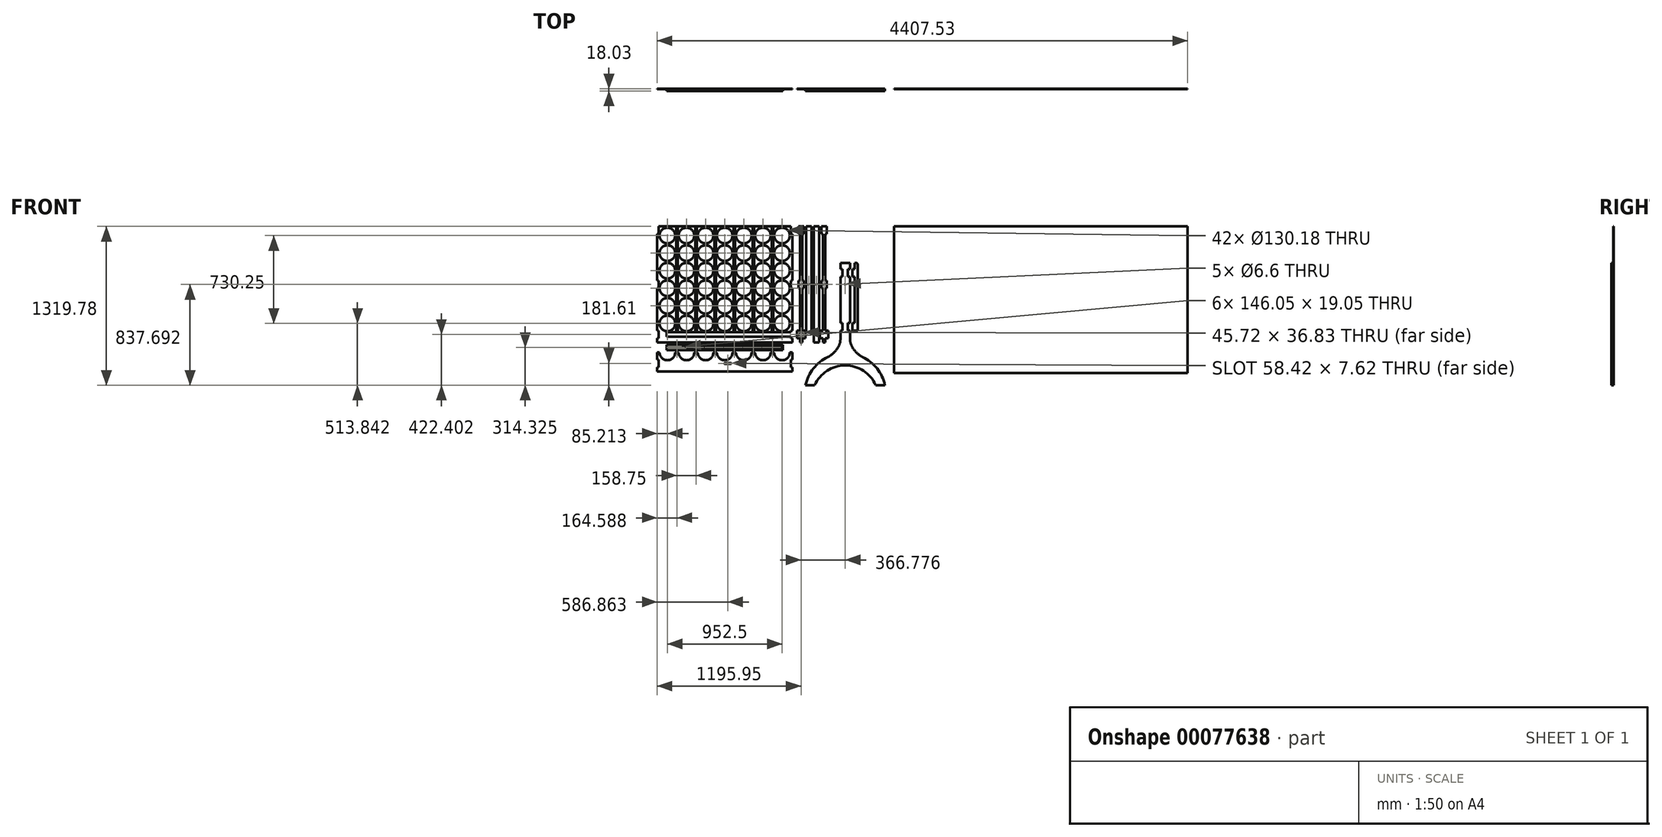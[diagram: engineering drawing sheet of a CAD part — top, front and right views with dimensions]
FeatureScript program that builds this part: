
annotation { "Feature Type Name" : "Feature", "Feature Type Description" : "" }
export const myFeature = defineFeature(function(context is Context, id is Id, definition is map)
    precondition{}
    {
        {
            assignVariable(context, id + "F0", {"name" : "Thickness", "anyValue" : .48});
        }
        {
            var Q0;
            Q0=qCreatedBy(makeId("Front.planeOp"),FACE);
            var sketch = newSketch(context, id + "F1", { "sketchPlane" : qUnion([Q0])});
            skLineSegment(sketch, "E0.bottom", {"start": v(-1389.63, 595.88) * mm, "end": v(-266.7, 595.88) * mm});
            skLineSegment(sketch, "E0.top", {"start": v(-1389.63, -368.3) * mm, "end": v(-266.7, -368.3) * mm});
            skLineSegment(sketch, "E0.left", {"start": v(-1389.63, 595.88) * mm, "end": v(-1389.63, -368.3) * mm});
            skLineSegment(sketch, "E0.right", {"start": v(-266.7, 595.88) * mm, "end": v(-266.7, -368.3) * mm});
            skCircle(sketch, "E1", {"center": v(-1304.42, 520.2) * mm, "radius": 65.09 * mm});
            skLineSegment(sketch, "E2.bottom", {"start": v(-1389.63, 595.88) * mm, "end": v(-1377.44, 595.88) * mm});
            skLineSegment(sketch, "E2.right", {"start": v(-1377.44, 595.88) * mm, "end": v(-1377.44, -368.3) * mm, "construction": true});
            skLineSegment(sketch, "E3.0", {"start": v(-278.9, 595.88) * mm, "end": v(-278.9, -368.3) * mm, "construction": true});
            skLineSegment(sketch, "E4.top", {"start": v(-1389.63, 532.38) * mm, "end": v(-1377.44, 532.38) * mm});
            skLineSegment(sketch, "E4.left", {"start": v(-1389.63, 595.88) * mm, "end": v(-1389.63, 532.38) * mm});
            skLineSegment(sketch, "E4.right", {"start": v(-1377.44, 595.88) * mm, "end": v(-1377.44, 532.38) * mm});
            skLineSegment(sketch, "E5.bottom", {"start": v(-266.7, 595.88) * mm, "end": v(-278.9, 595.88) * mm});
            skLineSegment(sketch, "E5.top", {"start": v(-266.7, 532.38) * mm, "end": v(-278.9, 532.38) * mm});
            skLineSegment(sketch, "E5.left", {"start": v(-266.7, 595.88) * mm, "end": v(-266.7, 532.38) * mm});
            skLineSegment(sketch, "E5.right", {"start": v(-278.9, 595.88) * mm, "end": v(-278.9, 532.38) * mm});
            skLineSegment(sketch, "E6.top", {"start": v(-266.7, -269.75) * mm, "end": v(-278.9, -269.75) * mm});
            skLineSegment(sketch, "E6.left", {"start": v(-266.7, -368.3) * mm, "end": v(-266.7, -269.75) * mm});
            skLineSegment(sketch, "E6.right", {"start": v(-278.9, -333.25) * mm, "end": v(-278.9, -269.75) * mm});
            skLineSegment(sketch, "E7.bottom", {"start": v(-1389.63, 145.54) * mm, "end": v(-1377.44, 145.54) * mm});
            skLineSegment(sketch, "E7.top", {"start": v(-1389.63, 82.04) * mm, "end": v(-1377.44, 82.04) * mm});
            skLineSegment(sketch, "E7.left", {"start": v(-1389.63, 145.54) * mm, "end": v(-1389.63, 82.04) * mm});
            skLineSegment(sketch, "E7.right", {"start": v(-1377.44, 145.54) * mm, "end": v(-1377.44, 82.04) * mm});
            skPoint(sketch, "E8", {"position": v(-1389.63, 113.8) * mm});
            skLineSegment(sketch, "E9.MirrorCS", {"start": v(-266.7, 82.04) * mm, "end": v(-278.9, 82.04) * mm});
            skLineSegment(sketch, "E10.MirrorCS", {"start": v(-266.7, 145.54) * mm, "end": v(-278.9, 145.54) * mm});
            skLineSegment(sketch, "E11.MirrorCS", {"start": v(-266.7, 145.54) * mm, "end": v(-266.7, 82.04) * mm});
            skLineSegment(sketch, "E12.MirrorCS", {"start": v(-278.9, 145.54) * mm, "end": v(-278.9, 82.04) * mm});
            skLineSegment(sketch, "E13", {"start": v(-1377.44, -283.08) * mm, "end": v(-278.9, -283.08) * mm});
            skLineSegment(sketch, "E14", {"start": v(-1231.4, 595.88) * mm, "end": v(-1231.4, -283.08) * mm});
            skLineSegment(sketch, "E15", {"start": v(-1218.7, 595.88) * mm, "end": v(-1218.7, -283.08) * mm});
            skLineSegment(sketch, "E16.1.0.0", {"start": v(-1059.94, 595.88) * mm, "end": v(-1059.94, -283.08) * mm});
            skLineSegment(sketch, "E16.1.0.1", {"start": v(-1072.64, 595.88) * mm, "end": v(-1072.64, -283.08) * mm});
            skLineSegment(sketch, "E16.2.0.0", {"start": v(-901.2, 595.88) * mm, "end": v(-901.2, -283.08) * mm});
            skLineSegment(sketch, "E16.2.0.1", {"start": v(-913.9, 595.88) * mm, "end": v(-913.9, -283.08) * mm});
            skLineSegment(sketch, "E16.3.0.0", {"start": v(-742.44, 595.88) * mm, "end": v(-742.44, -283.08) * mm});
            skLineSegment(sketch, "E16.3.0.1", {"start": v(-755.14, 595.88) * mm, "end": v(-755.14, -283.08) * mm});
            skLineSegment(sketch, "E16.4.0.0", {"start": v(-583.7, 595.88) * mm, "end": v(-583.7, -283.08) * mm});
            skLineSegment(sketch, "E16.4.0.1", {"start": v(-596.4, 595.88) * mm, "end": v(-596.4, -283.08) * mm});
            skLineSegment(sketch, "E16.5.0.0", {"start": v(-424.94, 595.88) * mm, "end": v(-424.94, -283.08) * mm});
            skLineSegment(sketch, "E16.5.0.1", {"start": v(-437.64, 595.88) * mm, "end": v(-437.64, -283.08) * mm});
            skLineSegment(sketch, "E16.direction1", {"start": v(-1218.7, -283.08) * mm, "end": v(-1059.94, -283.08) * mm, "construction": true});
            skLineSegment(sketch, "E17.bottom", {"start": v(-1304.42, -387.35) * mm, "end": v(-351.92, -387.35) * mm});
            skLineSegment(sketch, "E17.top", {"start": v(-1304.42, -431.8) * mm, "end": v(-351.92, -431.8) * mm});
            skLineSegment(sketch, "E17.left", {"start": v(-1304.42, -387.35) * mm, "end": v(-1304.42, -431.8) * mm, "construction": true});
            skLineSegment(sketch, "E17.right", {"start": v(-351.92, -387.35) * mm, "end": v(-351.92, -431.8) * mm, "construction": true});
            skLineSegment(sketch, "E18.bottom", {"start": v(-1298.07, -387.35) * mm, "end": v(-1310.77, -387.35) * mm});
            skLineSegment(sketch, "E18.top", {"start": v(-1298.07, -431.8) * mm, "end": v(-1310.77, -431.8) * mm});
            skLineSegment(sketch, "E18.left", {"start": v(-1298.07, -387.35) * mm, "end": v(-1298.07, -431.8) * mm});
            skLineSegment(sketch, "E18.right", {"start": v(-1310.77, -387.35) * mm, "end": v(-1310.77, -431.8) * mm});
            skPoint(sketch, "E18.middle", {"position": v(-1304.42, -409.57) * mm});
            skLineSegment(sketch, "E19.1.0.0", {"start": v(-1139.32, -387.35) * mm, "end": v(-1139.32, -431.8) * mm});
            skLineSegment(sketch, "E19.1.0.1", {"start": v(-1152.02, -387.35) * mm, "end": v(-1152.02, -431.8) * mm});
            skLineSegment(sketch, "E19.2.0.0", {"start": v(-980.57, -387.35) * mm, "end": v(-980.57, -431.8) * mm});
            skLineSegment(sketch, "E19.2.0.1", {"start": v(-993.27, -387.35) * mm, "end": v(-993.27, -431.8) * mm});
            skLineSegment(sketch, "E19.3.0.0", {"start": v(-821.82, -387.35) * mm, "end": v(-821.82, -431.8) * mm});
            skLineSegment(sketch, "E19.3.0.1", {"start": v(-834.52, -387.35) * mm, "end": v(-834.52, -431.8) * mm});
            skLineSegment(sketch, "E19.4.0.0", {"start": v(-663.07, -387.35) * mm, "end": v(-663.07, -431.8) * mm});
            skLineSegment(sketch, "E19.4.0.1", {"start": v(-675.77, -387.35) * mm, "end": v(-675.77, -431.8) * mm});
            skLineSegment(sketch, "E19.5.0.0", {"start": v(-504.32, -387.35) * mm, "end": v(-504.32, -431.8) * mm});
            skLineSegment(sketch, "E19.5.0.1", {"start": v(-517.02, -387.35) * mm, "end": v(-517.02, -431.8) * mm});
            skLineSegment(sketch, "E19.6.0.0", {"start": v(-345.57, -387.35) * mm, "end": v(-345.57, -431.8) * mm});
            skLineSegment(sketch, "E19.6.0.1", {"start": v(-358.27, -387.35) * mm, "end": v(-358.27, -431.8) * mm});
            skLineSegment(sketch, "E19.direction1", {"start": v(-1298.07, -431.8) * mm, "end": v(-1139.32, -431.8) * mm, "construction": true});
            skLineSegment(sketch, "E20", {"start": v(-345.57, -387.35) * mm, "end": v(-351.92, -387.35) * mm});
            skLineSegment(sketch, "E21", {"start": v(-321.75, -431.8) * mm, "end": v(-351.92, -431.8) * mm});
            skLineSegment(sketch, "E22", {"start": v(-1298.07, -409.58) * mm, "end": v(-1152.02, -409.58) * mm, "construction": true});
            skLineSegment(sketch, "E23.0", {"start": v(-1298.07, -419.1) * mm, "end": v(-1152.02, -419.1) * mm});
            skLineSegment(sketch, "E24.0", {"start": v(-1298.07, -400.05) * mm, "end": v(-1152.02, -400.05) * mm});
            skLineSegment(sketch, "E25.1.0.0", {"start": v(-1139.32, -400.05) * mm, "end": v(-993.27, -400.05) * mm});
            skLineSegment(sketch, "E25.1.0.1", {"start": v(-1139.32, -419.1) * mm, "end": v(-993.27, -419.1) * mm});
            skLineSegment(sketch, "E25.2.0.0", {"start": v(-980.57, -400.05) * mm, "end": v(-834.52, -400.05) * mm});
            skLineSegment(sketch, "E25.2.0.1", {"start": v(-980.57, -419.1) * mm, "end": v(-834.52, -419.1) * mm});
            skLineSegment(sketch, "E25.3.0.0", {"start": v(-821.82, -400.05) * mm, "end": v(-675.77, -400.05) * mm});
            skLineSegment(sketch, "E25.3.0.1", {"start": v(-821.82, -419.1) * mm, "end": v(-675.77, -419.1) * mm});
            skLineSegment(sketch, "E25.4.0.0", {"start": v(-663.07, -400.05) * mm, "end": v(-517.02, -400.05) * mm});
            skLineSegment(sketch, "E25.4.0.1", {"start": v(-663.07, -419.1) * mm, "end": v(-517.02, -419.1) * mm});
            skLineSegment(sketch, "E25.5.0.0", {"start": v(-504.32, -400.05) * mm, "end": v(-358.27, -400.05) * mm});
            skLineSegment(sketch, "E25.5.0.1", {"start": v(-504.32, -419.1) * mm, "end": v(-358.27, -419.1) * mm});
            skLineSegment(sketch, "E25.direction1", {"start": v(-1298.07, -400.05) * mm, "end": v(-1139.32, -400.05) * mm, "construction": true});
            skLineSegment(sketch, "E26.0", {"start": v(-1377.44, -319.91) * mm, "end": v(-278.9, -319.91) * mm});
            skLineSegment(sketch, "E27", {"start": v(-278.9, -333.25) * mm, "end": v(-266.7, -333.25) * mm});
            skLineSegment(sketch, "E28", {"start": v(-828.17, -368.3) * mm, "end": v(-828.17, -319.91) * mm, "construction": true});
            skLineSegment(sketch, "E29.MirrorCS", {"start": v(-1377.44, -333.25) * mm, "end": v(-1389.63, -333.25) * mm});
            skLineSegment(sketch, "E30.MirrorCS", {"start": v(-1377.44, -333.25) * mm, "end": v(-1377.44, -269.75) * mm});
            skLineSegment(sketch, "E31.MirrorCS", {"start": v(-1389.63, -269.75) * mm, "end": v(-1377.44, -269.75) * mm});
            skLineSegment(sketch, "E32", {"start": v(-1310.77, -319.91) * mm, "end": v(-1310.77, -283.08) * mm});
            skLineSegment(sketch, "E33.bottom", {"start": v(-215.9, 595.88) * mm, "end": v(-171.45, 595.88) * mm, "construction": true});
            skLineSegment(sketch, "E34.bottom", {"start": v(-228.1, -333.25) * mm, "end": v(-203.7, -333.25) * mm});
            skLineSegment(sketch, "E34.top", {"start": v(-228.1, -269.75) * mm, "end": v(-203.7, -269.75) * mm});
            skLineSegment(sketch, "E34.left", {"start": v(-228.1, -333.25) * mm, "end": v(-228.1, -269.75) * mm});
            skLineSegment(sketch, "E34.right", {"start": v(-203.7, -333.25) * mm, "end": v(-203.7, -269.75) * mm});
            skLineSegment(sketch, "E35", {"start": v(-193.68, -368.3) * mm, "end": v(-193.68, 595.88) * mm, "construction": true});
            skLineSegment(sketch, "E36.bottom", {"start": v(-215.9, 145.54) * mm, "end": v(-203.7, 145.54) * mm});
            skLineSegment(sketch, "E36.top", {"start": v(-215.9, 82.04) * mm, "end": v(-203.7, 82.04) * mm});
            skLineSegment(sketch, "E36.left", {"start": v(-215.9, 145.54) * mm, "end": v(-215.9, 82.04) * mm});
            skLineSegment(sketch, "E36.right", {"start": v(-203.7, 145.54) * mm, "end": v(-203.7, 82.04) * mm});
            skLineSegment(sketch, "E37.bottom", {"start": v(-215.9, 595.88) * mm, "end": v(-203.7, 595.88) * mm});
            skLineSegment(sketch, "E37.top", {"start": v(-215.9, 532.38) * mm, "end": v(-203.7, 532.38) * mm});
            skLineSegment(sketch, "E37.left", {"start": v(-215.9, 595.88) * mm, "end": v(-215.9, 532.38) * mm});
            skLineSegment(sketch, "E37.right", {"start": v(-203.7, 595.88) * mm, "end": v(-203.7, 532.38) * mm});
            skLineSegment(sketch, "E38.MirrorCS", {"start": v(-171.45, 595.88) * mm, "end": v(-171.45, 532.38) * mm});
            skLineSegment(sketch, "E39.MirrorCS", {"start": v(-171.45, 595.88) * mm, "end": v(-183.64, 595.88) * mm});
            skLineSegment(sketch, "E40.MirrorCS", {"start": v(-183.64, 595.88) * mm, "end": v(-183.64, 532.38) * mm});
            skLineSegment(sketch, "E41.MirrorCS", {"start": v(-171.45, 532.38) * mm, "end": v(-183.64, 532.38) * mm});
            skLineSegment(sketch, "E42.MirrorCS", {"start": v(-171.45, 145.54) * mm, "end": v(-171.45, 82.04) * mm});
            skLineSegment(sketch, "E43.MirrorCS", {"start": v(-171.45, 82.04) * mm, "end": v(-183.64, 82.04) * mm});
            skLineSegment(sketch, "E44.MirrorCS", {"start": v(-183.64, 145.54) * mm, "end": v(-183.64, 82.04) * mm});
            skLineSegment(sketch, "E45.MirrorCS", {"start": v(-171.45, 145.54) * mm, "end": v(-183.64, 145.54) * mm});
            skLineSegment(sketch, "E46.MirrorCS", {"start": v(-159.26, -333.25) * mm, "end": v(-159.26, -269.75) * mm});
            skLineSegment(sketch, "E47.MirrorCS", {"start": v(-159.26, -333.25) * mm, "end": v(-183.64, -333.25) * mm});
            skLineSegment(sketch, "E48.MirrorCS", {"start": v(-159.26, -269.75) * mm, "end": v(-183.64, -269.75) * mm});
            skLineSegment(sketch, "E49.MirrorCS", {"start": v(-183.64, -333.25) * mm, "end": v(-183.64, -269.75) * mm});
            skLineSegment(sketch, "E50.bottom", {"start": v(-203.7, -368.3) * mm, "end": v(-183.64, -368.3) * mm});
            skLineSegment(sketch, "E50.top", {"start": v(-203.7, 595.88) * mm, "end": v(-183.64, 595.88) * mm});
            skLineSegment(sketch, "E50.left", {"start": v(-203.7, -368.3) * mm, "end": v(-203.7, 595.88) * mm});
            skLineSegment(sketch, "E50.right", {"start": v(-183.64, -368.3) * mm, "end": v(-183.64, 595.88) * mm});
            skLineSegment(sketch, "E51.bottom", {"start": v(-216.54, -283.08) * mm, "end": v(-170.82, -283.08) * mm});
            skLineSegment(sketch, "E51.top", {"start": v(-216.54, -319.91) * mm, "end": v(-170.82, -319.91) * mm});
            skLineSegment(sketch, "E51.left", {"start": v(-216.54, -283.08) * mm, "end": v(-216.54, -319.91) * mm});
            skLineSegment(sketch, "E51.right", {"start": v(-170.82, -283.08) * mm, "end": v(-170.82, -319.91) * mm});
            skPoint(sketch, "E52", {"position": v(-193.68, -283.08) * mm});
            skLineSegment(sketch, "E53.bottom", {"start": v(-152.4, 595.88) * mm, "end": v(-107.95, 595.88) * mm});
            skLineSegment(sketch, "E53.top", {"start": v(-152.4, -368.3) * mm, "end": v(-107.95, -368.3) * mm, "construction": true});
            skLineSegment(sketch, "E53.left", {"start": v(-152.4, 595.88) * mm, "end": v(-152.4, -368.3) * mm});
            skLineSegment(sketch, "E53.right", {"start": v(-107.95, 595.88) * mm, "end": v(-107.95, -368.3) * mm});
            skLineSegment(sketch, "E54.0", {"start": v(-98.43, 532.38) * mm, "end": v(-98.43, -368.3) * mm, "construction": true});
            skLineSegment(sketch, "E55.MirrorCS", {"start": v(19.05, 595.88) * mm, "end": v(6.86, 595.88) * mm});
            skLineSegment(sketch, "E56.MirrorCS", {"start": v(-25.4, 595.88) * mm, "end": v(-13.2, 595.88) * mm});
            skLineSegment(sketch, "E57.MirrorCS", {"start": v(-37.6, -333.25) * mm, "end": v(-13.2, -333.25) * mm});
            skLineSegment(sketch, "E58.MirrorCS", {"start": v(31.24, -333.25) * mm, "end": v(6.86, -333.25) * mm});
            skLineSegment(sketch, "E59.MirrorCS", {"start": v(19.05, 82.04) * mm, "end": v(6.86, 82.04) * mm});
            skLineSegment(sketch, "E60.MirrorCS", {"start": v(19.05, 532.38) * mm, "end": v(6.86, 532.38) * mm});
            skLineSegment(sketch, "E61.MirrorCS", {"start": v(19.05, 595.88) * mm, "end": v(-25.4, 595.88) * mm, "construction": true});
            skLineSegment(sketch, "E62.MirrorCS", {"start": v(-37.6, -269.75) * mm, "end": v(-13.2, -269.75) * mm});
            skLineSegment(sketch, "E63.MirrorCS", {"start": v(-25.4, 532.38) * mm, "end": v(-13.2, 532.38) * mm});
            skLineSegment(sketch, "E64.MirrorCS", {"start": v(31.24, -269.75) * mm, "end": v(6.86, -269.75) * mm});
            skLineSegment(sketch, "E65.MirrorCS", {"start": v(-25.4, 82.04) * mm, "end": v(-13.2, 82.04) * mm});
            skLineSegment(sketch, "E66.MirrorCS", {"start": v(19.05, 145.54) * mm, "end": v(6.86, 145.54) * mm});
            skLineSegment(sketch, "E67.MirrorCS", {"start": v(-25.4, 145.54) * mm, "end": v(-13.2, 145.54) * mm});
            skLineSegment(sketch, "E68.MirrorCS", {"start": v(6.86, 595.88) * mm, "end": v(-13.2, 595.88) * mm});
            skLineSegment(sketch, "E69.MirrorCS", {"start": v(6.86, 145.54) * mm, "end": v(6.86, 82.04) * mm});
            skLineSegment(sketch, "E70.MirrorCS", {"start": v(-13.2, -333.25) * mm, "end": v(-13.2, -269.75) * mm});
            skLineSegment(sketch, "E71.MirrorCS", {"start": v(6.86, -368.3) * mm, "end": v(-13.2, -368.3) * mm});
            skLineSegment(sketch, "E72.MirrorCS", {"start": v(-44.45, -368.3) * mm, "end": v(-88.9, -368.3) * mm});
            skLineSegment(sketch, "E73.MirrorCS", {"start": v(-25.4, 145.54) * mm, "end": v(-25.4, 82.04) * mm});
            skLineSegment(sketch, "E74.MirrorCS", {"start": v(-13.2, 145.54) * mm, "end": v(-13.2, 82.04) * mm});
            skLineSegment(sketch, "E75.MirrorCS", {"start": v(6.86, -333.25) * mm, "end": v(6.86, -269.75) * mm});
            skLineSegment(sketch, "E76.MirrorCS", {"start": v(-37.6, -333.25) * mm, "end": v(-37.6, -269.75) * mm});
            skLineSegment(sketch, "E77.MirrorCS", {"start": v(19.05, 145.54) * mm, "end": v(19.05, 82.04) * mm});
            skLineSegment(sketch, "E78.MirrorCS", {"start": v(-13.2, -368.3) * mm, "end": v(-13.2, 595.88) * mm});
            skLineSegment(sketch, "E79.MirrorCS", {"start": v(-13.2, 595.88) * mm, "end": v(-13.2, 532.38) * mm});
            skPoint(sketch, "E80.MirrorP", {"position": v(-3.18, -283.08) * mm});
            skLineSegment(sketch, "E81.MirrorCS", {"start": v(-25.4, 595.88) * mm, "end": v(-25.4, 532.38) * mm});
            skLineSegment(sketch, "E82.MirrorCS", {"start": v(6.86, 595.88) * mm, "end": v(6.86, 532.38) * mm});
            skLineSegment(sketch, "E83.MirrorCS", {"start": v(19.05, 595.88) * mm, "end": v(19.05, 532.38) * mm});
            skLineSegment(sketch, "E84.MirrorCS", {"start": v(6.86, -368.3) * mm, "end": v(6.86, 595.88) * mm});
            skLineSegment(sketch, "E85.MirrorCS", {"start": v(31.24, -333.25) * mm, "end": v(31.24, -269.75) * mm});
            skLineSegment(sketch, "E86.MirrorCS", {"start": v(-44.45, 595.88) * mm, "end": v(-88.9, 595.88) * mm});
            skLineSegment(sketch, "E87.MirrorCS", {"start": v(-44.45, 595.88) * mm, "end": v(-44.45, -368.3) * mm});
            skLineSegment(sketch, "E88.MirrorCS", {"start": v(-88.9, 595.88) * mm, "end": v(-88.9, -368.3) * mm});
            skLineSegment(sketch, "E89.MirrorCS", {"start": v(-3.18, -368.3) * mm, "end": v(-3.18, 595.88) * mm, "construction": true});
            skLineSegment(sketch, "E90.bottom", {"start": v(-152.4, -283.08) * mm, "end": v(-107.95, -283.08) * mm});
            skLineSegment(sketch, "E90.top", {"start": v(-152.4, -319.91) * mm, "end": v(-107.95, -319.91) * mm, "construction": true});
            skLineSegment(sketch, "E90.left", {"start": v(-152.4, -283.08) * mm, "end": v(-152.4, -319.91) * mm});
            skLineSegment(sketch, "E90.right", {"start": v(-107.95, -283.08) * mm, "end": v(-107.95, -319.91) * mm});
            skLineSegment(sketch, "E91.bottom", {"start": v(-1389.63, -450.85) * mm, "end": v(-266.7, -450.85) * mm});
            skLineSegment(sketch, "E91.top", {"start": v(-1389.63, -609.1) * mm, "end": v(-266.7, -609.1) * mm});
            skLineSegment(sketch, "E91.left", {"start": v(-1389.63, -450.85) * mm, "end": v(-1389.63, -609.1) * mm});
            skLineSegment(sketch, "E91.right", {"start": v(-266.7, -450.85) * mm, "end": v(-266.7, -609.1) * mm});
            skLineSegment(sketch, "E92.bottom", {"start": v(132.84, -368.3) * mm, "end": v(213.36, -368.3) * mm, "construction": true});
            skLineSegment(sketch, "E92.top", {"start": v(132.84, 292.1) * mm, "end": v(213.36, 292.1) * mm});
            skLineSegment(sketch, "E92.left", {"start": v(132.84, -368.3) * mm, "end": v(132.84, 292.1) * mm});
            skLineSegment(sketch, "E92.right", {"start": v(213.36, -368.3) * mm, "end": v(213.36, 292.1) * mm});
            skLineSegment(sketch, "E93", {"start": v(132.84, -368.3) * mm, "end": v(37.01, -485.83) * mm});
            skLineSegment(sketch, "E94", {"start": v(-157.1, -723.9) * mm, "end": v(503.3, -723.9) * mm});
            skLineSegment(sketch, "E95", {"start": v(503.3, -723.9) * mm, "end": v(309.19, -485.83) * mm, "construction": true});
            skLineSegment(sketch, "E96", {"start": v(173.1, -368.3) * mm, "end": v(173.1, -723.9) * mm, "construction": true});
            skLineSegment(sketch, "E97.bottom", {"start": v(132.84, -269.75) * mm, "end": v(150.88, -269.75) * mm});
            skLineSegment(sketch, "E97.top", {"start": v(132.84, -206.25) * mm, "end": v(150.88, -206.25) * mm});
            skLineSegment(sketch, "E97.left", {"start": v(132.84, -269.75) * mm, "end": v(132.84, -206.25) * mm});
            skLineSegment(sketch, "E97.right", {"start": v(150.88, -269.75) * mm, "end": v(150.88, -206.25) * mm});
            skLineSegment(sketch, "E98.bottom", {"start": v(132.84, 241.3) * mm, "end": v(150.88, 241.3) * mm});
            skLineSegment(sketch, "E98.top", {"start": v(132.84, 177.8) * mm, "end": v(150.88, 177.8) * mm});
            skLineSegment(sketch, "E98.left", {"start": v(132.84, 241.3) * mm, "end": v(132.84, 177.8) * mm});
            skLineSegment(sketch, "E98.right", {"start": v(150.88, 241.3) * mm, "end": v(150.88, 177.8) * mm});
            skLineSegment(sketch, "E99.MirrorCS", {"start": v(213.36, -269.75) * mm, "end": v(195.33, -269.75) * mm});
            skLineSegment(sketch, "E100.MirrorCS", {"start": v(213.36, -206.25) * mm, "end": v(195.33, -206.25) * mm});
            skLineSegment(sketch, "E101.MirrorCS", {"start": v(213.36, -269.75) * mm, "end": v(213.36, -206.25) * mm});
            skLineSegment(sketch, "E102.MirrorCS", {"start": v(195.33, -269.75) * mm, "end": v(195.33, -206.25) * mm});
            skLineSegment(sketch, "E103.MirrorCS", {"start": v(213.36, 241.3) * mm, "end": v(213.36, 177.8) * mm});
            skLineSegment(sketch, "E104.MirrorCS", {"start": v(213.36, 177.8) * mm, "end": v(195.33, 177.8) * mm});
            skLineSegment(sketch, "E105.MirrorCS", {"start": v(195.33, 241.3) * mm, "end": v(195.33, 177.8) * mm});
            skLineSegment(sketch, "E106.MirrorCS", {"start": v(213.36, 241.3) * mm, "end": v(195.33, 241.3) * mm});
            skLineSegment(sketch, "E107.bottom", {"start": v(250.44, 292.1) * mm, "end": v(275.84, 292.1) * mm});
            skLineSegment(sketch, "E107.top", {"start": v(250.44, -269.75) * mm, "end": v(275.84, -269.75) * mm});
            skLineSegment(sketch, "E107.left", {"start": v(250.44, 292.1) * mm, "end": v(250.44, -269.75) * mm});
            skLineSegment(sketch, "E107.right", {"start": v(275.84, 292.1) * mm, "end": v(275.84, -269.75) * mm});
            skLineSegment(sketch, "E108.bottom", {"start": v(250.44, -269.75) * mm, "end": v(232.4, -269.75) * mm});
            skLineSegment(sketch, "E108.top", {"start": v(250.44, -206.25) * mm, "end": v(232.4, -206.25) * mm});
            skLineSegment(sketch, "E108.left", {"start": v(250.44, -269.75) * mm, "end": v(250.44, -206.25) * mm});
            skLineSegment(sketch, "E108.right", {"start": v(232.4, -269.75) * mm, "end": v(232.4, -206.25) * mm});
            skLineSegment(sketch, "E109.bottom", {"start": v(250.44, 241.3) * mm, "end": v(232.4, 241.3) * mm});
            skLineSegment(sketch, "E109.top", {"start": v(250.44, 177.8) * mm, "end": v(232.4, 177.8) * mm});
            skLineSegment(sketch, "E109.left", {"start": v(250.44, 241.3) * mm, "end": v(250.44, 177.8) * mm});
            skLineSegment(sketch, "E109.right", {"start": v(232.4, 241.3) * mm, "end": v(232.4, 177.8) * mm});
            skCircle(sketch, "E110", {"center": v(-3.18, 113.8) * mm, "radius": 3.3 * mm});
            skLineSegment(sketch, "E111", {"start": v(173.1, 292.1) * mm, "end": v(173.1, 113.8) * mm, "construction": true});
            skCircle(sketch, "E112", {"center": v(173.1, 113.8) * mm, "radius": 3.3 * mm});
            skCircle(sketch, "E113.MirrorC", {"center": v(-193.68, 113.8) * mm, "radius": 3.3 * mm});
            skCircle(sketch, "E114", {"center": v(-66.68, 113.8) * mm, "radius": 3.3 * mm});
            skPoint(sketch, "E114.centerSnap0", {"position": v(-25.4, 113.8) * mm});
            skPoint(sketch, "E114.centerSnap1", {"position": v(-66.68, 595.88) * mm});
            skCircle(sketch, "E115.MirrorC", {"center": v(-130.18, 113.8) * mm, "radius": 3.3 * mm});
            skLineSegment(sketch, "E116.top", {"start": v(-80.9, -711.2) * mm, "end": v(427.1, -711.2) * mm, "construction": true});
            skLineSegment(sketch, "E116.left", {"start": v(-80.9, -723.9) * mm, "end": v(-80.9, -711.2) * mm});
            skLineSegment(sketch, "E116.right", {"start": v(427.1, -723.9) * mm, "end": v(427.1, -711.2) * mm});
            skPoint(sketch, "E117", {"position": v(173.1, -711.2) * mm});
            skPoint(sketch, "E118", {"position": v(-130.18, -319.91) * mm});
            skLineSegment(sketch, "E119", {"start": v(-130.18, -368.3) * mm, "end": v(-130.18, -269.75) * mm, "construction": true});
            skArc(sketch, "E120", {"start": v(503.3, -723.9) * mm, "mid": v(173.1, -457.2) * mm, "end": v(-157.1, -723.9) * mm});
            skLineSegment(sketch, "E121", {"start": v(37.01, -485.83) * mm, "end": v(-157.1, -723.9) * mm, "construction": true});
            skLineSegment(sketch, "E122", {"start": v(309.19, -485.83) * mm, "end": v(213.36, -368.3) * mm});
            skArc(sketch, "E123", {"start": v(37.01, -485.83) * mm, "mid": v(94.77, -435.09) * mm, "end": v(132.84, -368.3) * mm});
            skArc(sketch, "E124", {"start": v(427.1, -723.9) * mm, "mid": v(173.1, -558.8) * mm, "end": v(-80.9, -723.9) * mm});
            skArc(sketch, "E125.MirrorCS", {"start": v(309.19, -485.83) * mm, "mid": v(251.43, -435.09) * mm, "end": v(213.36, -368.3) * mm});
            skArc(sketch, "E126.MirrorC", {"start": v(-445.58, -450.85) * mm, "mid": v(-510.67, -515.94) * mm, "end": v(-575.75, -450.85) * mm});
            skArc(sketch, "E127.MirrorC", {"start": v(-286.83, -450.85) * mm, "mid": v(-351.92, -515.94) * mm, "end": v(-417, -450.85) * mm});
            skArc(sketch, "E128.trimOffspring", {"start": v(-1239.33, -450.85) * mm, "mid": v(-1304.42, -515.94) * mm, "end": v(-1369.5, -450.85) * mm});
            skArc(sketch, "E129.trimOffspring", {"start": v(-1080.58, -450.85) * mm, "mid": v(-1145.67, -515.94) * mm, "end": v(-1210.75, -450.85) * mm});
            skArc(sketch, "E130.trimOffspring", {"start": v(-921.83, -450.85) * mm, "mid": v(-986.92, -515.94) * mm, "end": v(-1052, -450.85) * mm});
            skArc(sketch, "E131.trimOffspring", {"start": v(-763.08, -450.85) * mm, "mid": v(-828.17, -515.94) * mm, "end": v(-893.25, -450.85) * mm});
            skArc(sketch, "E132.trimOffspring", {"start": v(-604.33, -450.85) * mm, "mid": v(-669.42, -515.94) * mm, "end": v(-734.5, -450.85) * mm});
            skLineSegment(sketch, "E133.bottom", {"start": v(-1389.63, -510.54) * mm, "end": v(-1376.43, -510.54) * mm});
            skLineSegment(sketch, "E133.top", {"start": v(-1389.63, -450.85) * mm, "end": v(-1376.43, -450.85) * mm});
            skLineSegment(sketch, "E133.left", {"start": v(-1389.63, -510.54) * mm, "end": v(-1389.63, -450.85) * mm, "construction": true});
            skLineSegment(sketch, "E133.right", {"start": v(-1376.43, -510.54) * mm, "end": v(-1376.43, -450.85) * mm});
            skLineSegment(sketch, "E134.bottom", {"start": v(-1389.63, -450.85) * mm, "end": v(-1401.83, -450.85) * mm, "construction": true});
            skLineSegment(sketch, "E134.top", {"start": v(-1389.63, -510.54) * mm, "end": v(-1401.83, -510.54) * mm, "construction": true});
            skLineSegment(sketch, "E134.left", {"start": v(-1389.63, -450.85) * mm, "end": v(-1389.63, -510.54) * mm, "construction": true});
            skLineSegment(sketch, "E134.right", {"start": v(-1401.83, -450.85) * mm, "end": v(-1401.83, -510.54) * mm, "construction": true});
            skLineSegment(sketch, "E135.MirrorCS", {"start": v(-279.9, -510.54) * mm, "end": v(-279.9, -450.85) * mm});
            skLineSegment(sketch, "E136", {"start": v(-279.9, -510.54) * mm, "end": v(-266.7, -510.54) * mm});
            skLineSegment(sketch, "E137.top", {"start": v(-279.9, -574.04) * mm, "end": v(-266.7, -574.04) * mm});
            skLineSegment(sketch, "E137.left", {"start": v(-279.9, -510.54) * mm, "end": v(-279.9, -574.04) * mm});
            skLineSegment(sketch, "E137.right", {"start": v(-266.7, -510.54) * mm, "end": v(-266.7, -574.04) * mm});
            skLineSegment(sketch, "E138.MirrorCS", {"start": v(-1376.43, -510.54) * mm, "end": v(-1376.43, -574.04) * mm});
            skLineSegment(sketch, "E139.MirrorCS", {"start": v(-1376.43, -574.04) * mm, "end": v(-1389.63, -574.04) * mm});
            skLineSegment(sketch, "E140", {"start": v(-828.17, -542.29) * mm, "end": v(-777.37, -542.29) * mm});
            skArc(sketch, "E141.0.startCap", {"start": v(-828.17, -546.1) * mm, "mid": v(-831.98, -542.29) * mm, "end": v(-828.17, -538.48) * mm});
            skArc(sketch, "E141.0.endCap", {"start": v(-777.37, -538.48) * mm, "mid": v(-773.56, -542.29) * mm, "end": v(-777.37, -546.1) * mm});
            skLineSegment(sketch, "E141.0.left", {"start": v(-828.17, -538.48) * mm, "end": v(-777.37, -538.48) * mm});
            skLineSegment(sketch, "E141.0.right", {"start": v(-828.17, -546.1) * mm, "end": v(-777.37, -546.1) * mm});
            skCircle(sketch, "E142.0.1.0", {"center": v(-1304.42, 374.14) * mm, "radius": 65.09 * mm});
            skCircle(sketch, "E142.0.2.0", {"center": v(-1304.42, 228.1) * mm, "radius": 65.09 * mm});
            skCircle(sketch, "E142.0.3.0", {"center": v(-1304.42, 82.04) * mm, "radius": 65.09 * mm});
            skCircle(sketch, "E142.0.4.0", {"center": v(-1304.42, -64) * mm, "radius": 65.09 * mm});
            skCircle(sketch, "E142.0.5.0", {"center": v(-1304.42, -210.06) * mm, "radius": 65.09 * mm});
            skCircle(sketch, "E142.1.0.0", {"center": v(-1145.67, 520.2) * mm, "radius": 65.09 * mm});
            skCircle(sketch, "E142.1.1.0", {"center": v(-1145.67, 374.14) * mm, "radius": 65.09 * mm});
            skCircle(sketch, "E142.1.2.0", {"center": v(-1145.67, 228.1) * mm, "radius": 65.09 * mm});
            skCircle(sketch, "E142.1.3.0", {"center": v(-1145.67, 82.04) * mm, "radius": 65.09 * mm});
            skCircle(sketch, "E142.1.4.0", {"center": v(-1145.67, -64) * mm, "radius": 65.09 * mm});
            skCircle(sketch, "E142.1.5.0", {"center": v(-1145.67, -210.06) * mm, "radius": 65.09 * mm});
            skCircle(sketch, "E142.2.0.0", {"center": v(-986.92, 520.2) * mm, "radius": 65.09 * mm});
            skCircle(sketch, "E142.2.1.0", {"center": v(-986.92, 374.14) * mm, "radius": 65.09 * mm});
            skCircle(sketch, "E142.2.2.0", {"center": v(-986.92, 228.1) * mm, "radius": 65.09 * mm});
            skCircle(sketch, "E142.2.3.0", {"center": v(-986.92, 82.04) * mm, "radius": 65.09 * mm});
            skCircle(sketch, "E142.2.4.0", {"center": v(-986.92, -64) * mm, "radius": 65.09 * mm});
            skCircle(sketch, "E142.2.5.0", {"center": v(-986.92, -210.06) * mm, "radius": 65.09 * mm});
            skCircle(sketch, "E142.3.0.0", {"center": v(-828.17, 520.2) * mm, "radius": 65.09 * mm});
            skCircle(sketch, "E142.3.1.0", {"center": v(-828.17, 374.14) * mm, "radius": 65.09 * mm});
            skCircle(sketch, "E142.3.2.0", {"center": v(-828.17, 228.1) * mm, "radius": 65.09 * mm});
            skCircle(sketch, "E142.3.3.0", {"center": v(-828.17, 82.04) * mm, "radius": 65.09 * mm});
            skCircle(sketch, "E142.3.4.0", {"center": v(-828.17, -64) * mm, "radius": 65.09 * mm});
            skCircle(sketch, "E142.3.5.0", {"center": v(-828.17, -210.06) * mm, "radius": 65.09 * mm});
            skCircle(sketch, "E142.4.0.0", {"center": v(-669.42, 520.2) * mm, "radius": 65.09 * mm});
            skCircle(sketch, "E142.4.1.0", {"center": v(-669.42, 374.14) * mm, "radius": 65.09 * mm});
            skCircle(sketch, "E142.4.2.0", {"center": v(-669.42, 228.1) * mm, "radius": 65.09 * mm});
            skCircle(sketch, "E142.4.3.0", {"center": v(-669.42, 82.04) * mm, "radius": 65.09 * mm});
            skCircle(sketch, "E142.4.4.0", {"center": v(-669.42, -64) * mm, "radius": 65.09 * mm});
            skCircle(sketch, "E142.4.5.0", {"center": v(-669.42, -210.06) * mm, "radius": 65.09 * mm});
            skCircle(sketch, "E142.5.0.0", {"center": v(-510.67, 520.2) * mm, "radius": 65.09 * mm});
            skCircle(sketch, "E142.5.1.0", {"center": v(-510.67, 374.14) * mm, "radius": 65.09 * mm});
            skCircle(sketch, "E142.5.2.0", {"center": v(-510.67, 228.1) * mm, "radius": 65.09 * mm});
            skCircle(sketch, "E142.5.3.0", {"center": v(-510.67, 82.04) * mm, "radius": 65.09 * mm});
            skCircle(sketch, "E142.5.4.0", {"center": v(-510.67, -64) * mm, "radius": 65.09 * mm});
            skCircle(sketch, "E142.5.5.0", {"center": v(-510.67, -210.06) * mm, "radius": 65.09 * mm});
            skCircle(sketch, "E142.6.0.0", {"center": v(-351.92, 520.2) * mm, "radius": 65.09 * mm});
            skCircle(sketch, "E142.6.1.0", {"center": v(-351.92, 374.14) * mm, "radius": 65.09 * mm});
            skCircle(sketch, "E142.6.2.0", {"center": v(-351.92, 228.1) * mm, "radius": 65.09 * mm});
            skCircle(sketch, "E142.6.3.0", {"center": v(-351.92, 82.04) * mm, "radius": 65.09 * mm});
            skCircle(sketch, "E142.6.4.0", {"center": v(-351.92, -64) * mm, "radius": 65.09 * mm});
            skCircle(sketch, "E142.6.5.0", {"center": v(-351.92, -210.06) * mm, "radius": 65.09 * mm});
            skLineSegment(sketch, "E142.direction1", {"start": v(-1304.42, 520.2) * mm, "end": v(-1145.67, 520.2) * mm, "construction": true});
            skLineSegment(sketch, "E142.direction2", {"start": v(-1304.42, 520.2) * mm, "end": v(-1304.42, 374.14) * mm, "construction": true});
            skCircle(sketch, "E143", {"center": v(-1304.42, -210.06) * mm, "radius": 73.03 * mm, "construction": true});
            skLineSegment(sketch, "E144.bottom", {"start": v(579.5, 595.88) * mm, "end": v(3017.9, 595.88) * mm});
            skLineSegment(sketch, "E144.top", {"start": v(579.5, -623.32) * mm, "end": v(3017.9, -623.32) * mm});
            skLineSegment(sketch, "E144.left", {"start": v(579.5, 595.88) * mm, "end": v(579.5, -623.32) * mm});
            skLineSegment(sketch, "E144.right", {"start": v(3017.9, 595.88) * mm, "end": v(3017.9, -623.32) * mm});
            skPoint(sketch, "E145", {"position": v(-1310.77, -301.5) * mm});
            skLineSegment(sketch, "E146", {"start": v(-278.9, -283.08) * mm, "end": v(-278.9, -319.91) * mm});
            skPoint(sketch, "E147", {"position": v(-278.9, -301.5) * mm});
            skLineSegment(sketch, "E148", {"start": v(-1310.77, -301.5) * mm, "end": v(-1310.77, -368.3) * mm, "construction": true});
            skLineSegment(sketch, "E149", {"start": v(-1376.43, -542.3) * mm, "end": v(-1376.43, -609.1) * mm, "construction": true});
            skSolve(sketch);
        }
        {
            var Q0;
            Q0=makeQuery(id+"F1.imprint","IMPRINT",FACE,{"disambiguationData":[TD([[makeQuery(id+"F1.imprint","IMPRINT",EDGE,{"derivedFrom":sQuery(id+"F1.wireOp",EDGE,"b72d2d66-4ce2-4289-90ab-e637a022988c.0.6.0")}),-1.0]])]});
            var Q1;
            Q1=makeQuery(id+"F1.imprint","IMPRINT",FACE,{"disambiguationData":[TD([[makeQuery(id+"F1.imprint","IMPRINT",EDGE,{"derivedFrom":sQuery(id+"F1.wireOp",EDGE,"E1")}),-1.0]])]});
            var Q2;
            Q2=makeQuery(id+"F1.imprint","IMPRINT",FACE,{"disambiguationData":[TD([[makeQuery(id+"F1.imprint","IMPRINT",EDGE,{"derivedFrom":sQuery(id+"F1.wireOp",EDGE,"e17ad13c-0773-4227-a656-80a7ee0610df.1.0.0")}),-1.0]])]});
            var Q3;
            Q3=makeQuery(id+"F1.imprint","IMPRINT",FACE,{"disambiguationData":[TD([[makeQuery(id+"F1.imprint","IMPRINT",EDGE,{"derivedFrom":sQuery(id+"F1.wireOp",EDGE,"e17ad13c-0773-4227-a656-80a7ee0610df.2.0.0")}),-1.0]])]});
            var Q4;
            Q4=makeQuery(id+"F1.imprint","IMPRINT",FACE,{"disambiguationData":[TD([[makeQuery(id+"F1.imprint","IMPRINT",EDGE,{"derivedFrom":sQuery(id+"F1.wireOp",EDGE,"e17ad13c-0773-4227-a656-80a7ee0610df.3.0.0")}),-1.0]])]});
            var Q5;
            Q5=makeQuery(id+"F1.imprint","IMPRINT",FACE,{"disambiguationData":[TD([[makeQuery(id+"F1.imprint","IMPRINT",EDGE,{"derivedFrom":sQuery(id+"F1.wireOp",EDGE,"e17ad13c-0773-4227-a656-80a7ee0610df.4.0.0")}),-1.0]])]});
            var Q6;
            Q6=makeQuery(id+"F1.imprint","IMPRINT",FACE,{"disambiguationData":[TD([[makeQuery(id+"F1.imprint","IMPRINT",EDGE,{"derivedFrom":sQuery(id+"F1.wireOp",EDGE,"e17ad13c-0773-4227-a656-80a7ee0610df.5.0.0")}),-1.0]])]});
            var Q7;
            Q7=makeQuery(id+"F1.imprint","IMPRINT",FACE,{"disambiguationData":[TD([[makeQuery(id+"F1.imprint","IMPRINT",EDGE,{"derivedFrom":sQuery(id+"F1.wireOp",EDGE,"XpdAvdAL-t41n-kh1d-zuyA-r62Oe6xQwDXB")}),-1.0]])]});
            var Q8;
            Q8=makeQuery(id+"F1.imprint","IMPRINT",FACE,{"disambiguationData":[TD([[makeQuery(id+"F1.imprint","IMPRINT",EDGE,{"derivedFrom":sQuery(id+"F1.wireOp",EDGE,"c9cc7f5d-6211-4dc9-b41b-aaae2feddd97.1.0.0")}),-1.0]])]});
            var Q9;
            Q9=makeQuery(id+"F1.imprint","IMPRINT",FACE,{"disambiguationData":[TD([[makeQuery(id+"F1.imprint","IMPRINT",EDGE,{"derivedFrom":sQuery(id+"F1.wireOp",EDGE,"c9cc7f5d-6211-4dc9-b41b-aaae2feddd97.2.0.0")}),-1.0]])]});
            var Q10;
            Q10=makeQuery(id+"F1.imprint","IMPRINT",FACE,{"disambiguationData":[TD([[makeQuery(id+"F1.imprint","IMPRINT",EDGE,{"derivedFrom":sQuery(id+"F1.wireOp",EDGE,"c9cc7f5d-6211-4dc9-b41b-aaae2feddd97.3.0.0")}),-1.0]])]});
            var Q11;
            Q11=makeQuery(id+"F1.imprint","IMPRINT",FACE,{"disambiguationData":[TD([[makeQuery(id+"F1.imprint","IMPRINT",EDGE,{"derivedFrom":sQuery(id+"F1.wireOp",EDGE,"c9cc7f5d-6211-4dc9-b41b-aaae2feddd97.4.0.0")}),-1.0]])]});
            var Q12;
            Q12=makeQuery(id+"F1.imprint","IMPRINT",FACE,{"disambiguationData":[TD([[makeQuery(id+"F1.imprint","IMPRINT",EDGE,{"derivedFrom":sQuery(id+"F1.wireOp",EDGE,"c9cc7f5d-6211-4dc9-b41b-aaae2feddd97.5.0.0")}),-1.0]])]});
            var Q13;
            {var subQ0=sQuery(id+"F1.wireOp",EDGE,"e9a3ff06-c462-4903-9302-cb255ffcaa57.0.5.0");Q13=makeQuery(id+"F1.imprint","IMPRINT",FACE,{"disambiguationData":[TD([[makeQuery(id+"F1.imprint","IMPRINT",EDGE,{"derivedFrom":subQ0}),1.0]])]});}
            var Q14;
            {var subQ0=sQuery(id+"F1.wireOp",EDGE,"E0.top");Q14=makeQuery(id+"F1.imprint","IMPRINT",FACE,{"disambiguationData":[TD([[makeQuery(id+"F1.imprint","IMPRINT",EDGE,{"derivedFrom":subQ0}),1.0]])]});}
            var Q15;
            {var subQ0=sQuery(id+"F1.wireOp",EDGE,"zuuYGtIx-YfND-we87-dVk1-2TNHSHCjCdNj.top");Q15=makeQuery(id+"F1.imprint","IMPRINT",FACE,{"disambiguationData":[TD([[makeQuery(id+"F1.imprint","IMPRINT",EDGE,{"derivedFrom":subQ0}),1.0]])]});}
            var Q16;
            Q16=makeQuery(id+"F1.imprint","IMPRINT",FACE,{"disambiguationData":[TD([[makeQuery(id+"F1.imprint","IMPRINT",EDGE,{"derivedFrom":sQuery(id+"F1.wireOp",EDGE,"RaYTgRfS-HCax-OzBH-qsnV-oxM8qn66qDHo.bottom")}),-1.0]])]});
            var Q17;
            Q17=makeQuery(id+"F1.imprint","IMPRINT",FACE,{"disambiguationData":[TD([[makeQuery(id+"F1.imprint","IMPRINT",EDGE,{"derivedFrom":sQuery(id+"F1.wireOp",EDGE,"A2z6aU3x-cg6c-CzpY-Q7PS-y1Ii9rqkyWUI.bottom")}),-1.0]])]});
            var Q18;
            Q18=makeQuery(id+"F1.imprint","IMPRINT",FACE,{"disambiguationData":[TD([[makeQuery(id+"F1.imprint","IMPRINT",EDGE,{"derivedFrom":sQuery(id+"F1.wireOp",EDGE,"7ee9f5a2-2083-4d3d-b315-0f95102f96d621.MirrorC")}),1.0]])]});
            var Q19;
            Q19=makeQuery(id+"F1.imprint","IMPRINT",FACE,{"disambiguationData":[TD([[makeQuery(id+"F1.imprint","IMPRINT",EDGE,{"derivedFrom":sQuery(id+"F1.wireOp",EDGE,"7ee9f5a2-2083-4d3d-b315-0f95102f96d60.MirrorCS")}),1.0]])]});
            var Q20;
            {var subQ8=sQuery(id+"F1.wireOp",EDGE,"3cc9daea-cbba-44d1-9671-21d01c85290615.MirrorCS");Q20=makeQuery(id+"F1.imprint","IMPRINT",FACE,{"disambiguationData":[TD([[makeQuery(id+"F1.imprint","IMPRINT",EDGE,{"derivedFrom":subQ8}),-1.0]])]});}
            var Q21;
            Q21=makeQuery(id+"F1.imprint","IMPRINT",FACE,{"disambiguationData":[TD([[makeQuery(id+"F1.imprint","IMPRINT",EDGE,{"derivedFrom":sQuery(id+"F1.wireOp",EDGE,"3cc9daea-cbba-44d1-9671-21d01c85290657.MirrorCS")}),1.0]])]});
            var Q22;
            Q22=makeQuery(id+"F1.imprint","IMPRINT",FACE,{"disambiguationData":[TD([[makeQuery(id+"F1.imprint","IMPRINT",EDGE,{"derivedFrom":sQuery(id+"F1.wireOp",EDGE,"3cc9daea-cbba-44d1-9671-21d01c85290645.MirrorCS")}),1.0]])]});
            var Q23;
            Q23=makeQuery(id+"F1.imprint","IMPRINT",FACE,{"disambiguationData":[TD([[makeQuery(id+"F1.imprint","IMPRINT",EDGE,{"derivedFrom":sQuery(id+"F1.wireOp",EDGE,"3cc9daea-cbba-44d1-9671-21d01c85290633.MirrorC")}),1.0]])]});
            var Q24;
            Q24=makeQuery(id+"F1.imprint","IMPRINT",FACE,{"disambiguationData":[TD([[makeQuery(id+"F1.imprint","IMPRINT",EDGE,{"derivedFrom":sQuery(id+"F1.wireOp",EDGE,"3cc9daea-cbba-44d1-9671-21d01c85290625.MirrorCS")}),-1.0]])]});
            var Q25;
            {var subQ1=sQuery(id+"F1.wireOp",EDGE,"3cc9daea-cbba-44d1-9671-21d01c85290614.MirrorCS");Q25=makeQuery(id+"F1.imprint","IMPRINT",FACE,{"disambiguationData":[TD([[makeQuery(id+"F1.imprint","IMPRINT",EDGE,{"derivedFrom":subQ1}),1.0]])]});}
            var Q26;
            {var subQ1=sQuery(id+"F1.wireOp",EDGE,"3cc9daea-cbba-44d1-9671-21d01c85290616.MirrorCS");var subQ3=sQuery(id+"F1.wireOp",EDGE,"3cc9daea-cbba-44d1-9671-21d01c85290618.MirrorCS");var subQ4=makeQuery(id+"F1.imprint","INTERSECT",VERTEX,{"derivedFrom":[subQ1,subQ3]});Q26=makeQuery(id+"F1.imprint","IMPRINT",FACE,{"disambiguationData":[TD([[makeQuery(id+"F1.imprint","IMPRINT",EDGE,{"disambiguationData":[TD([[subQ4,-1.0]])],"derivedFrom":subQ3}),1.0]])]});}
            var Q27;
            {var subQ2=sQuery(id+"F1.wireOp",EDGE,"3cc9daea-cbba-44d1-9671-21d01c85290632.MirrorCS");Q27=makeQuery(id+"F1.imprint","IMPRINT",FACE,{"disambiguationData":[TD([[makeQuery(id+"F1.imprint","IMPRINT",EDGE,{"derivedFrom":subQ2}),-1.0]])]});}
            var Q28;
            {var subQ2=sQuery(id+"F1.wireOp",EDGE,"3cc9daea-cbba-44d1-9671-21d01c85290615.MirrorCS");Q28=makeQuery(id+"F1.imprint","IMPRINT",FACE,{"disambiguationData":[TD([[makeQuery(id+"F1.imprint","IMPRINT",EDGE,{"derivedFrom":subQ2}),1.0]])]});}
            var Q29;
            Q29=makeQuery(id+"F1.imprint","IMPRINT",FACE,{"disambiguationData":[TD([[makeQuery(id+"F1.imprint","IMPRINT",EDGE,{"derivedFrom":sQuery(id+"F1.wireOp",EDGE,"7ee9f5a2-2083-4d3d-b315-0f95102f96d68.MirrorCS")}),1.0]])]});
            var Q30;
            Q30=makeQuery(id+"F1.imprint","IMPRINT",FACE,{"disambiguationData":[TD([[makeQuery(id+"F1.imprint","IMPRINT",EDGE,{"derivedFrom":sQuery(id+"F1.wireOp",EDGE,"7ee9f5a2-2083-4d3d-b315-0f95102f96d66.MirrorCS")}),1.0]])]});
            var Q31;
            {var subQ1=sQuery(id+"F1.wireOp",EDGE,"Ql8xjKSZ-osiJ-ou1O-RUti-zKqZGMklHdmG.bottom");Q31=makeQuery(id+"F1.imprint","IMPRINT",FACE,{"disambiguationData":[TD([[makeQuery(id+"F1.imprint","IMPRINT",EDGE,{"derivedFrom":subQ1}),-1.0]])]});}
            var Q32;
            {var subQ1=sQuery(id+"F1.wireOp",EDGE,"vNJjCRz3-f4OO-4W7b-yauL-aWNgJRgR4KzO.bottom");Q32=makeQuery(id+"F1.imprint","IMPRINT",FACE,{"disambiguationData":[TD([[makeQuery(id+"F1.imprint","IMPRINT",EDGE,{"derivedFrom":subQ1}),1.0]])]});}
            var Q33;
            {var subQ0=sQuery(id+"F1.wireOp",EDGE,"RaYTgRfS-HCax-OzBH-qsnV-oxM8qn66qDHo.top");Q33=makeQuery(id+"F1.imprint","IMPRINT",FACE,{"disambiguationData":[TD([[makeQuery(id+"F1.imprint","IMPRINT",EDGE,{"derivedFrom":subQ0}),1.0]])]});}
            var Q34;
            Q34=makeQuery(id+"F1.imprint","IMPRINT",FACE,{"disambiguationData":[TD([[makeQuery(id+"F1.imprint","IMPRINT",EDGE,{"derivedFrom":sQuery(id+"F1.wireOp",EDGE,"MePqlvqW-R92V-4SML-vUzJ-x8LzeLdQ50hA.bottom")}),-1.0]])]});
            var Q35;
            Q35=makeQuery(id+"F1.imprint","IMPRINT",FACE,{"disambiguationData":[TD([[makeQuery(id+"F1.imprint","IMPRINT",EDGE,{"derivedFrom":sQuery(id+"F1.wireOp",EDGE,"eToSEdLw-ZPEH-Me9I-LjQH-tnaRYInkmE1b.bottom")}),1.0]])]});
            var Q36;
            Q36=makeQuery(id+"F1.imprint","IMPRINT",FACE,{"disambiguationData":[TD([[makeQuery(id+"F1.imprint","IMPRINT",EDGE,{"derivedFrom":sQuery(id+"F1.wireOp",EDGE,"7ee9f5a2-2083-4d3d-b315-0f95102f96d64.MirrorCS")}),-1.0]])]});
            var Q37;
            Q37=makeQuery(id+"F1.imprint","IMPRINT",FACE,{"disambiguationData":[TD([[makeQuery(id+"F1.imprint","IMPRINT",EDGE,{"derivedFrom":sQuery(id+"F1.wireOp",EDGE,"7ee9f5a2-2083-4d3d-b315-0f95102f96d62.MirrorCS")}),1.0]])]});
            var Q38;
            Q38=makeQuery(id+"F1.imprint","IMPRINT",FACE,{"disambiguationData":[TD([[makeQuery(id+"F1.imprint","IMPRINT",EDGE,{"derivedFrom":sQuery(id+"F1.wireOp",EDGE,"3cc9daea-cbba-44d1-9671-21d01c85290613.MirrorCS")}),1.0]])]});
            var Q39;
            Q39=makeQuery(id+"F1.imprint","IMPRINT",FACE,{"disambiguationData":[TD([[makeQuery(id+"F1.imprint","IMPRINT",EDGE,{"derivedFrom":sQuery(id+"F1.wireOp",EDGE,"3cc9daea-cbba-44d1-9671-21d01c85290642.MirrorCS")}),-1.0]])]});
            var Q40;
            Q40=makeQuery(id+"F1.imprint","IMPRINT",FACE,{"disambiguationData":[TD([[makeQuery(id+"F1.imprint","IMPRINT",EDGE,{"derivedFrom":sQuery(id+"F1.wireOp",EDGE,"3cc9daea-cbba-44d1-9671-21d01c85290620.MirrorCS")}),-1.0]])]});
            var Q41;
            Q41=makeQuery(id+"F1.imprint","IMPRINT",FACE,{"disambiguationData":[TD([[makeQuery(id+"F1.imprint","IMPRINT",EDGE,{"derivedFrom":sQuery(id+"F1.wireOp",EDGE,"3cc9daea-cbba-44d1-9671-21d01c85290621.MirrorCS")}),-1.0]])]});
            var Q42;
            Q42=makeQuery(id+"F1.imprint","IMPRINT",FACE,{"disambiguationData":[TD([[makeQuery(id+"F1.imprint","IMPRINT",EDGE,{"derivedFrom":sQuery(id+"F1.wireOp",EDGE,"8i7omnKA-XiQc-A4SL-4TcC-43kh4ndWTDuy.bottom")}),-1.0]])]});
            var Q43;
            {var subQ0=sQuery(id+"F1.wireOp",EDGE,"7ee9f5a2-2083-4d3d-b315-0f95102f96d610.MirrorCS");Q43=makeQuery(id+"F1.imprint","IMPRINT",FACE,{"disambiguationData":[TD([[makeQuery(id+"F1.imprint","IMPRINT",EDGE,{"derivedFrom":subQ0}),1.0]])]});}
            var Q44;
            {var subQ0=sQuery(id+"F1.wireOp",EDGE,"7ee9f5a2-2083-4d3d-b315-0f95102f96d65.MirrorCS");Q44=makeQuery(id+"F1.imprint","IMPRINT",FACE,{"disambiguationData":[TD([[makeQuery(id+"F1.imprint","IMPRINT",EDGE,{"derivedFrom":subQ0}),1.0]])]});}
            var Q45;
            {var subQ0=sQuery(id+"F1.wireOp",EDGE,"3cc9daea-cbba-44d1-9671-21d01c85290626.MirrorCS");Q45=makeQuery(id+"F1.imprint","IMPRINT",FACE,{"disambiguationData":[TD([[makeQuery(id+"F1.imprint","IMPRINT",EDGE,{"derivedFrom":subQ0}),-1.0]])]});}
            var Q46;
            {var subQ0=sQuery(id+"F1.wireOp",EDGE,"3cc9daea-cbba-44d1-9671-21d01c8529068.MirrorCS");Q46=makeQuery(id+"F1.imprint","IMPRINT",FACE,{"disambiguationData":[TD([[makeQuery(id+"F1.imprint","IMPRINT",EDGE,{"derivedFrom":subQ0}),1.0]])]});}
            var Q47;
            {var subQ0=sQuery(id+"F1.wireOp",EDGE,"3cc9daea-cbba-44d1-9671-21d01c85290640.MirrorCS");Q47=makeQuery(id+"F1.imprint","IMPRINT",FACE,{"disambiguationData":[TD([[makeQuery(id+"F1.imprint","IMPRINT",EDGE,{"derivedFrom":subQ0}),1.0]])]});}
            var Q48;
            {var subQ0=sQuery(id+"F1.wireOp",EDGE,"3cc9daea-cbba-44d1-9671-21d01c85290612.MirrorCS");Q48=makeQuery(id+"F1.imprint","IMPRINT",FACE,{"disambiguationData":[TD([[makeQuery(id+"F1.imprint","IMPRINT",EDGE,{"derivedFrom":subQ0}),-1.0]])]});}
            var Q49;
            Q49=makeQuery(id+"F1.imprint","IMPRINT",FACE,{"disambiguationData":[TD([[makeQuery(id+"F1.imprint","IMPRINT",EDGE,{"derivedFrom":sQuery(id+"F1.wireOp",EDGE,"pkzA8YXS-147m-h1o3-BIs2-CFvluc7HSHoC.bottom")}),1.0]])]});
            var Q50;
            {var subQ5=sQuery(id+"F1.wireOp",EDGE,"43f020bf-c188-477f-bb01-5622551f1bd82.MirrorCS");Q50=makeQuery(id+"F1.imprint","IMPRINT",FACE,{"disambiguationData":[TD([[makeQuery(id+"F1.imprint","IMPRINT",EDGE,{"derivedFrom":subQ5}),1.0]])]});}
            var Q51;
            Q51=makeQuery(id+"F1.imprint","IMPRINT",FACE,{"disambiguationData":[TD([[makeQuery(id+"F1.imprint","IMPRINT",EDGE,{"derivedFrom":sQuery(id+"F1.wireOp",EDGE,"FgWoepQM-oAc9-YKjo-rVyh-H2xzB4l6eYAx.bottom")}),-1.0]])]});
            var Q52;
            Q52=makeQuery(id+"F1.imprint","IMPRINT",FACE,{"disambiguationData":[TD([[makeQuery(id+"F1.imprint","IMPRINT",EDGE,{"derivedFrom":sQuery(id+"F1.wireOp",EDGE,"nsbAEkxb-gdlj-1fSG-6ZRn-gvIsFKBOcmSa.top")}),1.0]])]});
            var Q53;
            Q53=makeQuery(id+"F1.imprint","IMPRINT",FACE,{"disambiguationData":[TD([[makeQuery(id+"F1.imprint","IMPRINT",EDGE,{"derivedFrom":sQuery(id+"F1.wireOp",EDGE,"7ab01751-0d8d-4895-afa0-6445531c586e.1.0.1")}),-1.0]])]});
            var Q54;
            Q54=makeQuery(id+"F1.imprint","IMPRINT",FACE,{"disambiguationData":[TD([[makeQuery(id+"F1.imprint","IMPRINT",EDGE,{"derivedFrom":sQuery(id+"F1.wireOp",EDGE,"7ab01751-0d8d-4895-afa0-6445531c586e.2.0.1")}),-1.0]])]});
            var Q55;
            Q55=makeQuery(id+"F1.imprint","IMPRINT",FACE,{"disambiguationData":[TD([[makeQuery(id+"F1.imprint","IMPRINT",EDGE,{"derivedFrom":sQuery(id+"F1.wireOp",EDGE,"7ab01751-0d8d-4895-afa0-6445531c586e.3.0.1")}),-1.0]])]});
            var Q56;
            Q56=makeQuery(id+"F1.imprint","IMPRINT",FACE,{"disambiguationData":[TD([[makeQuery(id+"F1.imprint","IMPRINT",EDGE,{"derivedFrom":sQuery(id+"F1.wireOp",EDGE,"7ab01751-0d8d-4895-afa0-6445531c586e.4.0.1")}),-1.0]])]});
            var Q57;
            Q57=makeQuery(id+"F1.imprint","IMPRINT",FACE,{"disambiguationData":[TD([[makeQuery(id+"F1.imprint","IMPRINT",EDGE,{"derivedFrom":sQuery(id+"F1.wireOp",EDGE,"7ab01751-0d8d-4895-afa0-6445531c586e.5.0.1")}),-1.0]])]});
            var Q58;
            Q58=makeQuery(id+"F1.imprint","IMPRINT",FACE,{"disambiguationData":[TD([[makeQuery(id+"F1.imprint","IMPRINT",EDGE,{"derivedFrom":sQuery(id+"F1.wireOp",EDGE,"49cf5ac7-3a91-41c2-95b4-914cce5436a2.1.6.0")}),-1.0]])]});
            var Q59;
            {var subQ2=sQuery(id+"F1.wireOp",EDGE,"Y7vdvrbU-9VXp-oTm6-BqFg-j6OfKwPQvjlB");Q59=makeQuery(id+"F1.imprint","IMPRINT",FACE,{"disambiguationData":[TD([[makeQuery(id+"F1.imprint","IMPRINT",EDGE,{"derivedFrom":subQ2}),-1.0]])]});}
            var Q60;
            {var subQ9=sQuery(id+"F1.wireOp",EDGE,"E5.top");Q60=makeQuery(id+"F1.imprint","IMPRINT",FACE,{"disambiguationData":[TD([[makeQuery(id+"F1.imprint","IMPRINT",EDGE,{"derivedFrom":subQ9}),1.0]])]});}
            var Q61;
            {var subQ0=sQuery(id+"F1.wireOp",EDGE,"E37.bottom");Q61=makeQuery(id+"F1.imprint","IMPRINT",FACE,{"disambiguationData":[TD([[makeQuery(id+"F1.imprint","IMPRINT",EDGE,{"derivedFrom":subQ0}),-1.0]])]});}
            var Q62;
            {var subQ9=sQuery(id+"F1.wireOp",EDGE,"E50.top");Q62=makeQuery(id+"F1.imprint","IMPRINT",FACE,{"disambiguationData":[TD([[makeQuery(id+"F1.imprint","IMPRINT",EDGE,{"derivedFrom":subQ9}),-1.0]])]});}
            var Q63;
            Q63=makeQuery(id+"F1.imprint","IMPRINT",FACE,{"disambiguationData":[TD([[makeQuery(id+"F1.imprint","IMPRINT",EDGE,{"derivedFrom":sQuery(id+"F1.wireOp",EDGE,"E38.MirrorCS")}),-1.0]])]});
            var Q64;
            Q64=makeQuery(id+"F1.imprint","IMPRINT",FACE,{"disambiguationData":[TD([[makeQuery(id+"F1.imprint","IMPRINT",EDGE,{"derivedFrom":sQuery(id+"F1.wireOp",EDGE,"E53.bottom")}),-1.0]])]});
            var Q65;
            Q65=makeQuery(id+"F1.imprint","IMPRINT",FACE,{"disambiguationData":[TD([[makeQuery(id+"F1.imprint","IMPRINT",EDGE,{"derivedFrom":sQuery(id+"F1.wireOp",EDGE,"E72.MirrorCS")}),-1.0]])]});
            var Q66;
            Q66=makeQuery(id+"F1.imprint","IMPRINT",FACE,{"disambiguationData":[TD([[makeQuery(id+"F1.imprint","IMPRINT",EDGE,{"derivedFrom":sQuery(id+"F1.wireOp",EDGE,"E56.MirrorCS")}),-1.0]])]});
            var Q67;
            {var subQ12=sQuery(id+"F1.wireOp",EDGE,"E68.MirrorCS");Q67=makeQuery(id+"F1.imprint","IMPRINT",FACE,{"disambiguationData":[TD([[makeQuery(id+"F1.imprint","IMPRINT",EDGE,{"derivedFrom":subQ12}),1.0]])]});}
            var Q68;
            {var subQ0=sQuery(id+"F1.wireOp",EDGE,"E55.MirrorCS");Q68=makeQuery(id+"F1.imprint","IMPRINT",FACE,{"disambiguationData":[TD([[makeQuery(id+"F1.imprint","IMPRINT",EDGE,{"derivedFrom":subQ0}),1.0]])]});}
            var Q69;
            {var subQ0=sQuery(id+"F1.wireOp",EDGE,"E36.bottom");Q69=makeQuery(id+"F1.imprint","IMPRINT",FACE,{"disambiguationData":[TD([[makeQuery(id+"F1.imprint","IMPRINT",EDGE,{"derivedFrom":subQ0}),-1.0]])]});}
            var Q70;
            Q70=makeQuery(id+"F1.imprint","IMPRINT",FACE,{"disambiguationData":[TD([[makeQuery(id+"F1.imprint","IMPRINT",EDGE,{"derivedFrom":sQuery(id+"F1.wireOp",EDGE,"E42.MirrorCS")}),-1.0]])]});
            var Q71;
            {var subQ0=sQuery(id+"F1.wireOp",EDGE,"E65.MirrorCS");Q71=makeQuery(id+"F1.imprint","IMPRINT",FACE,{"disambiguationData":[TD([[makeQuery(id+"F1.imprint","IMPRINT",EDGE,{"derivedFrom":subQ0}),1.0]])]});}
            var Q72;
            {var subQ0=sQuery(id+"F1.wireOp",EDGE,"E59.MirrorCS");Q72=makeQuery(id+"F1.imprint","IMPRINT",FACE,{"disambiguationData":[TD([[makeQuery(id+"F1.imprint","IMPRINT",EDGE,{"derivedFrom":subQ0}),-1.0]])]});}
            var Q73;
            {var subQ2=sQuery(id+"F1.wireOp",EDGE,"E50.bottom");Q73=makeQuery(id+"F1.imprint","IMPRINT",FACE,{"disambiguationData":[TD([[makeQuery(id+"F1.imprint","IMPRINT",EDGE,{"derivedFrom":subQ2}),1.0]])]});}
            var Q74;
            {var subQ0=sQuery(id+"F1.wireOp",EDGE,"E58.MirrorCS");Q74=makeQuery(id+"F1.imprint","IMPRINT",FACE,{"disambiguationData":[TD([[makeQuery(id+"F1.imprint","IMPRINT",EDGE,{"derivedFrom":subQ0}),-1.0]])]});}
            var Q75;
            {var subQ0=sQuery(id+"F1.wireOp",EDGE,"E57.MirrorCS");Q75=makeQuery(id+"F1.imprint","IMPRINT",FACE,{"disambiguationData":[TD([[makeQuery(id+"F1.imprint","IMPRINT",EDGE,{"derivedFrom":subQ0}),1.0]])]});}
            var Q76;
            {var subQ3=sQuery(id+"F1.wireOp",EDGE,"E32");Q76=makeQuery(id+"F1.imprint","IMPRINT",FACE,{"disambiguationData":[TD([[makeQuery(id+"F1.imprint","IMPRINT",EDGE,{"derivedFrom":subQ3}),1.0]])]});}
            var Q77;
            Q77=makeQuery(id+"F1.imprint","IMPRINT",FACE,{"disambiguationData":[TD([[makeQuery(id+"F1.imprint","IMPRINT",EDGE,{"derivedFrom":sQuery(id+"F1.wireOp",EDGE,"E46.MirrorCS")}),1.0]])]});
            var Q78;
            Q78=makeQuery(id+"F1.imprint","IMPRINT",FACE,{"disambiguationData":[TD([[makeQuery(id+"F1.imprint","IMPRINT",EDGE,{"derivedFrom":sQuery(id+"F1.wireOp",EDGE,"E91.bottom")}),-1.0]])]});
            var Q79;
            Q79=makeQuery(id+"F1.imprint","IMPRINT",FACE,{"disambiguationData":[TD([[makeQuery(id+"F1.imprint","IMPRINT",EDGE,{"derivedFrom":sQuery(id+"F1.wireOp",EDGE,"E91.left")}),-1.0]])]});
            var Q80;
            Q80=makeQuery(id+"F1.imprint","IMPRINT",FACE,{"disambiguationData":[TD([[makeQuery(id+"F1.imprint","IMPRINT",EDGE,{"derivedFrom":sQuery(id+"F1.wireOp",EDGE,"E91.right")}),1.0]])]});
            var Q81;
            {var subQ9=sQuery(id+"F1.wireOp",EDGE,"aa94eb73-4e7f-4a9c-8df9-c293ded4868a13.MirrorCS");Q81=makeQuery(id+"F1.imprint","IMPRINT",FACE,{"disambiguationData":[TD([[makeQuery(id+"F1.imprint","IMPRINT",EDGE,{"derivedFrom":subQ9}),-1.0]])]});}
            var Q82;
            {var subQ2=sQuery(id+"F1.wireOp",EDGE,"aa94eb73-4e7f-4a9c-8df9-c293ded4868a35.MirrorCS");Q82=makeQuery(id+"F1.imprint","IMPRINT",FACE,{"disambiguationData":[TD([[makeQuery(id+"F1.imprint","IMPRINT",EDGE,{"derivedFrom":subQ2}),1.0]])]});}
            var Q83;
            {var subQ1=sQuery(id+"F1.wireOp",EDGE,"aa94eb73-4e7f-4a9c-8df9-c293ded4868a31.MirrorCS");Q83=makeQuery(id+"F1.imprint","IMPRINT",FACE,{"disambiguationData":[TD([[makeQuery(id+"F1.imprint","IMPRINT",EDGE,{"derivedFrom":subQ1}),-1.0]])]});}
            var Q84;
            {var subQ1=sQuery(id+"F1.wireOp",EDGE,"aa94eb73-4e7f-4a9c-8df9-c293ded4868a39.MirrorCS");Q84=makeQuery(id+"F1.imprint","IMPRINT",FACE,{"disambiguationData":[TD([[makeQuery(id+"F1.imprint","IMPRINT",EDGE,{"derivedFrom":subQ1}),-1.0]])]});}
            var Q85;
            Q85=makeQuery(id+"F1.imprint","IMPRINT",FACE,{"disambiguationData":[TD([[makeQuery(id+"F1.imprint","IMPRINT",EDGE,{"derivedFrom":sQuery(id+"F1.wireOp",EDGE,"aa94eb73-4e7f-4a9c-8df9-c293ded4868a33.MirrorC")}),1.0]])]});
            var Q86;
            Q86=makeQuery(id+"F1.imprint","IMPRINT",FACE,{"disambiguationData":[TD([[makeQuery(id+"F1.imprint","IMPRINT",EDGE,{"derivedFrom":sQuery(id+"F1.wireOp",EDGE,"aa94eb73-4e7f-4a9c-8df9-c293ded4868a52.MirrorC")}),1.0]])]});
            var Q87;
            {var subQ5=sQuery(id+"F1.wireOp",EDGE,"aa94eb73-4e7f-4a9c-8df9-c293ded4868a3.MirrorCS");Q87=makeQuery(id+"F1.imprint","IMPRINT",FACE,{"disambiguationData":[TD([[makeQuery(id+"F1.imprint","IMPRINT",EDGE,{"derivedFrom":subQ5}),-1.0]])]});}
            var Q88;
            {var subQ5=sQuery(id+"F1.wireOp",EDGE,"aa94eb73-4e7f-4a9c-8df9-c293ded4868a24.MirrorCS");Q88=makeQuery(id+"F1.imprint","IMPRINT",FACE,{"disambiguationData":[TD([[makeQuery(id+"F1.imprint","IMPRINT",EDGE,{"derivedFrom":subQ5}),-1.0]])]});}
            var Q89;
            {var subQ5=sQuery(id+"F1.wireOp",EDGE,"aa94eb73-4e7f-4a9c-8df9-c293ded4868a4.MirrorCS");Q89=makeQuery(id+"F1.imprint","IMPRINT",FACE,{"disambiguationData":[TD([[makeQuery(id+"F1.imprint","IMPRINT",EDGE,{"derivedFrom":subQ5}),1.0]])]});}
            var Q90;
            {var subQ0=sQuery(id+"F1.wireOp",EDGE,"E15");Q90=makeQuery(id+"F1.imprint","IMPRINT",FACE,{"disambiguationData":[TD([[makeQuery(id+"F1.imprint","IMPRINT",EDGE,{"derivedFrom":subQ0}),1.0]])]});}
            var Q91;
            {var subQ0=sQuery(id+"F1.wireOp",EDGE,"E16.1.0.0");Q91=makeQuery(id+"F1.imprint","IMPRINT",FACE,{"disambiguationData":[TD([[makeQuery(id+"F1.imprint","IMPRINT",EDGE,{"derivedFrom":subQ0}),1.0]])]});}
            var Q92;
            {var subQ0=sQuery(id+"F1.wireOp",EDGE,"E16.2.0.0");Q92=makeQuery(id+"F1.imprint","IMPRINT",FACE,{"disambiguationData":[TD([[makeQuery(id+"F1.imprint","IMPRINT",EDGE,{"derivedFrom":subQ0}),1.0]])]});}
            var Q93;
            {var subQ0=sQuery(id+"F1.wireOp",EDGE,"E16.3.0.0");Q93=makeQuery(id+"F1.imprint","IMPRINT",FACE,{"disambiguationData":[TD([[makeQuery(id+"F1.imprint","IMPRINT",EDGE,{"derivedFrom":subQ0}),1.0]])]});}
            var Q94;
            {var subQ0=sQuery(id+"F1.wireOp",EDGE,"E16.4.0.0");Q94=makeQuery(id+"F1.imprint","IMPRINT",FACE,{"disambiguationData":[TD([[makeQuery(id+"F1.imprint","IMPRINT",EDGE,{"derivedFrom":subQ0}),1.0]])]});}
            var Q95;
            {var subQ1=sQuery(id+"F1.wireOp",EDGE,"E34.top");Q95=makeQuery(id+"F1.imprint","IMPRINT",FACE,{"disambiguationData":[TD([[makeQuery(id+"F1.imprint","IMPRINT",EDGE,{"derivedFrom":subQ1}),-1.0]])]});}
            var Q96;
            {var subQ2=sQuery(id+"F1.wireOp",EDGE,"E133.bottom");Q96=makeQuery(id+"F1.imprint","IMPRINT",FACE,{"disambiguationData":[TD([[makeQuery(id+"F1.imprint","IMPRINT",EDGE,{"derivedFrom":subQ2}),1.0]])]});}
            var Q97;
            {var subQ3=sQuery(id+"F1.wireOp",EDGE,"E135.MirrorCS");Q97=makeQuery(id+"F1.imprint","IMPRINT",FACE,{"disambiguationData":[TD([[makeQuery(id+"F1.imprint","IMPRINT",EDGE,{"derivedFrom":subQ3}),-1.0]])]});}
            var Q98;
            Q98=makeQuery(id+"F1.imprint","IMPRINT",FACE,{"disambiguationData":[TD([[makeQuery(id+"F1.imprint","IMPRINT",EDGE,{"derivedFrom":sQuery(id+"F1.wireOp",EDGE,"E144.bottom")}),-1.0]])]});
            extrude(context, id + "F2", {"entities" : qUnion([Q0, Q1, Q2, Q3, Q4, Q5, Q6, Q7, Q8, Q9, Q10, Q11, Q12, Q13, Q14, Q15, Q16, Q17, Q18, Q19, Q20, Q21, Q22, Q23, Q24, Q25, Q26, Q27, Q28, Q29, Q30, Q31, Q32, Q33, Q34, Q35, Q36, Q37, Q38, Q39, Q40, Q41, Q42, Q43, Q44, Q45, Q46, Q47, Q48, Q49, Q50, Q51, Q52, Q53, Q54, Q55, Q56, Q57, Q58, Q59, Q60, Q61, Q62, Q63, Q64, Q65, Q66, Q67, Q68, Q69, Q70, Q71, Q72, Q73, Q74, Q75, Q76, Q77, Q78, Q79, Q80, Q81, Q82, Q83, Q84, Q85, Q86, Q87, Q88, Q89, Q90, Q91, Q92, Q93, Q94, Q95, Q96, Q97, Q98]), "depth" : (getVariable(context, 'Thickness')) * mm});
        }
        {
            var Q0;
            Q0=makeQuery(id+"F1.imprint","IMPRINT",FACE,{"disambiguationData":[TD([[makeQuery(id+"F1.imprint","IMPRINT",EDGE,{"derivedFrom":sQuery(id+"F1.wireOp",EDGE,"63688b75-6c1a-4b18-8993-3e2f64380d1d.0.startCap")}),1.0]])]});
            var Q1;
            {var subQ0=sQuery(id+"F1.wireOp",EDGE,"E14");Q1=makeQuery(id+"F1.imprint","IMPRINT",FACE,{"disambiguationData":[TD([[makeQuery(id+"F1.imprint","IMPRINT",EDGE,{"derivedFrom":subQ0}),1.0]])]});}
            var Q2;
            {var subQ0=sQuery(id+"F1.wireOp",EDGE,"E16.1.0.0");Q2=makeQuery(id+"F1.imprint","IMPRINT",FACE,{"disambiguationData":[TD([[makeQuery(id+"F1.imprint","IMPRINT",EDGE,{"derivedFrom":subQ0}),-1.0]])]});}
            var Q3;
            {var subQ0=sQuery(id+"F1.wireOp",EDGE,"E16.2.0.0");Q3=makeQuery(id+"F1.imprint","IMPRINT",FACE,{"disambiguationData":[TD([[makeQuery(id+"F1.imprint","IMPRINT",EDGE,{"derivedFrom":subQ0}),-1.0]])]});}
            var Q4;
            {var subQ0=sQuery(id+"F1.wireOp",EDGE,"E16.3.0.0");Q4=makeQuery(id+"F1.imprint","IMPRINT",FACE,{"disambiguationData":[TD([[makeQuery(id+"F1.imprint","IMPRINT",EDGE,{"derivedFrom":subQ0}),-1.0]])]});}
            var Q5;
            {var subQ0=sQuery(id+"F1.wireOp",EDGE,"E16.4.0.0");Q5=makeQuery(id+"F1.imprint","IMPRINT",FACE,{"disambiguationData":[TD([[makeQuery(id+"F1.imprint","IMPRINT",EDGE,{"derivedFrom":subQ0}),-1.0]])]});}
            var Q6;
            {var subQ0=sQuery(id+"F1.wireOp",EDGE,"E16.5.0.0");Q6=makeQuery(id+"F1.imprint","IMPRINT",FACE,{"disambiguationData":[TD([[makeQuery(id+"F1.imprint","IMPRINT",EDGE,{"derivedFrom":subQ0}),-1.0]])]});}
            var Q7;
            {var subQ0=sQuery(id+"F1.wireOp",EDGE,"E16.6.0.0");Q7=makeQuery(id+"F1.imprint","IMPRINT",FACE,{"disambiguationData":[TD([[makeQuery(id+"F1.imprint","IMPRINT",EDGE,{"derivedFrom":subQ0}),-1.0]])]});}
            var Q8;
            {var subQ0=sQuery(id+"F1.wireOp",EDGE,"aa94eb73-4e7f-4a9c-8df9-c293ded4868a79.MirrorCS");Q8=makeQuery(id+"F1.imprint","IMPRINT",FACE,{"disambiguationData":[TD([[makeQuery(id+"F1.imprint","IMPRINT",EDGE,{"derivedFrom":subQ0}),-1.0]])]});}
            var Q9;
            {var subQ0=sQuery(id+"F1.wireOp",EDGE,"aa94eb73-4e7f-4a9c-8df9-c293ded4868a31.MirrorCS");Q9=makeQuery(id+"F1.imprint","IMPRINT",FACE,{"disambiguationData":[TD([[makeQuery(id+"F1.imprint","IMPRINT",EDGE,{"derivedFrom":subQ0}),1.0]])]});}
            var Q10;
            {var subQ0=sQuery(id+"F1.wireOp",EDGE,"aa94eb73-4e7f-4a9c-8df9-c293ded4868a39.MirrorCS");Q10=makeQuery(id+"F1.imprint","IMPRINT",FACE,{"disambiguationData":[TD([[makeQuery(id+"F1.imprint","IMPRINT",EDGE,{"derivedFrom":subQ0}),1.0]])]});}
            var Q11;
            {var subQ0=sQuery(id+"F1.wireOp",EDGE,"aa94eb73-4e7f-4a9c-8df9-c293ded4868a46.MirrorCS");Q11=makeQuery(id+"F1.imprint","IMPRINT",FACE,{"disambiguationData":[TD([[makeQuery(id+"F1.imprint","IMPRINT",EDGE,{"derivedFrom":subQ0}),1.0]])]});}
            var Q12;
            {var subQ0=sQuery(id+"F1.wireOp",EDGE,"aa94eb73-4e7f-4a9c-8df9-c293ded4868a54.MirrorCS");Q12=makeQuery(id+"F1.imprint","IMPRINT",FACE,{"disambiguationData":[TD([[makeQuery(id+"F1.imprint","IMPRINT",EDGE,{"derivedFrom":subQ0}),1.0]])]});}
            var Q13;
            {var subQ0=sQuery(id+"F1.wireOp",EDGE,"aa94eb73-4e7f-4a9c-8df9-c293ded4868a60.MirrorCS");Q13=makeQuery(id+"F1.imprint","IMPRINT",FACE,{"disambiguationData":[TD([[makeQuery(id+"F1.imprint","IMPRINT",EDGE,{"derivedFrom":subQ0}),1.0]])]});}
            extrude(context, id + "F3", {"entities" : qUnion([Q0, Q1, Q2, Q3, Q4, Q5, Q6, Q7, Q8, Q9, Q10, Q11, Q12, Q13]), "operationType" : NewBodyOperationType.ADD, "depth" : (getVariable(context, 'Thickness') / 2) * mm});
        }
        {
            var Q0;
            {var subQ7=sQuery(id+"F1.wireOp",EDGE,"E18.right");Q0=makeQuery(id+"F1.imprint","IMPRINT",FACE,{"disambiguationData":[TD([[makeQuery(id+"F1.imprint","IMPRINT",EDGE,{"derivedFrom":subQ7}),1.0]])]});}
            var Q1;
            {var subQ5=sQuery(id+"F1.wireOp",EDGE,"E24.0");Q1=makeQuery(id+"F1.imprint","IMPRINT",FACE,{"disambiguationData":[TD([[makeQuery(id+"F1.imprint","IMPRINT",EDGE,{"derivedFrom":subQ5}),1.0]])]});}
            var Q2;
            {var subQ5=sQuery(id+"F1.wireOp",EDGE,"E23.0");Q2=makeQuery(id+"F1.imprint","IMPRINT",FACE,{"disambiguationData":[TD([[makeQuery(id+"F1.imprint","IMPRINT",EDGE,{"derivedFrom":subQ5}),-1.0]])]});}
            var Q3;
            {var subQ0=sQuery(id+"F1.wireOp",EDGE,"E19.1.0.0");var subQ1=sQuery(id+"F1.wireOp",EDGE,"E17.bottom");var subQ2=makeQuery(id+"F1.imprint","INTERSECT",VERTEX,{"derivedFrom":[subQ1,subQ0]});Q3=makeQuery(id+"F1.imprint","IMPRINT",FACE,{"disambiguationData":[TD([[makeQuery(id+"F1.imprint","IMPRINT",EDGE,{"disambiguationData":[TD([[subQ2,1.0]])],"derivedFrom":subQ1}),-1.0]])]});}
            var Q4;
            {var subQ5=sQuery(id+"F1.wireOp",EDGE,"E25.1.0.0");Q4=makeQuery(id+"F1.imprint","IMPRINT",FACE,{"disambiguationData":[TD([[makeQuery(id+"F1.imprint","IMPRINT",EDGE,{"derivedFrom":subQ5}),1.0]])]});}
            var Q5;
            {var subQ5=sQuery(id+"F1.wireOp",EDGE,"E25.1.0.1");Q5=makeQuery(id+"F1.imprint","IMPRINT",FACE,{"disambiguationData":[TD([[makeQuery(id+"F1.imprint","IMPRINT",EDGE,{"derivedFrom":subQ5}),-1.0]])]});}
            var Q6;
            {var subQ0=sQuery(id+"F1.wireOp",EDGE,"E19.2.0.0");var subQ7=sQuery(id+"F1.wireOp",EDGE,"E17.bottom");var subQ8=makeQuery(id+"F1.imprint","INTERSECT",VERTEX,{"derivedFrom":[subQ7,subQ0]});Q6=makeQuery(id+"F1.imprint","IMPRINT",FACE,{"disambiguationData":[TD([[makeQuery(id+"F1.imprint","IMPRINT",EDGE,{"disambiguationData":[TD([[subQ8,1.0]])],"derivedFrom":subQ7}),-1.0]])]});}
            var Q7;
            {var subQ5=sQuery(id+"F1.wireOp",EDGE,"E25.2.0.0");Q7=makeQuery(id+"F1.imprint","IMPRINT",FACE,{"disambiguationData":[TD([[makeQuery(id+"F1.imprint","IMPRINT",EDGE,{"derivedFrom":subQ5}),1.0]])]});}
            var Q8;
            {var subQ5=sQuery(id+"F1.wireOp",EDGE,"E25.2.0.1");Q8=makeQuery(id+"F1.imprint","IMPRINT",FACE,{"disambiguationData":[TD([[makeQuery(id+"F1.imprint","IMPRINT",EDGE,{"derivedFrom":subQ5}),-1.0]])]});}
            var Q9;
            {var subQ0=sQuery(id+"F1.wireOp",EDGE,"E19.3.0.0");var subQ3=sQuery(id+"F1.wireOp",EDGE,"E17.bottom");var subQ4=makeQuery(id+"F1.imprint","INTERSECT",VERTEX,{"derivedFrom":[subQ3,subQ0]});Q9=makeQuery(id+"F1.imprint","IMPRINT",FACE,{"disambiguationData":[TD([[makeQuery(id+"F1.imprint","IMPRINT",EDGE,{"disambiguationData":[TD([[subQ4,1.0]])],"derivedFrom":subQ3}),-1.0]])]});}
            var Q10;
            {var subQ5=sQuery(id+"F1.wireOp",EDGE,"E25.3.0.0");Q10=makeQuery(id+"F1.imprint","IMPRINT",FACE,{"disambiguationData":[TD([[makeQuery(id+"F1.imprint","IMPRINT",EDGE,{"derivedFrom":subQ5}),1.0]])]});}
            var Q11;
            {var subQ5=sQuery(id+"F1.wireOp",EDGE,"E25.3.0.1");Q11=makeQuery(id+"F1.imprint","IMPRINT",FACE,{"disambiguationData":[TD([[makeQuery(id+"F1.imprint","IMPRINT",EDGE,{"derivedFrom":subQ5}),-1.0]])]});}
            var Q12;
            {var subQ0=sQuery(id+"F1.wireOp",EDGE,"E19.4.0.0");var subQ3=sQuery(id+"F1.wireOp",EDGE,"E17.bottom");var subQ4=makeQuery(id+"F1.imprint","INTERSECT",VERTEX,{"derivedFrom":[subQ3,subQ0]});Q12=makeQuery(id+"F1.imprint","IMPRINT",FACE,{"disambiguationData":[TD([[makeQuery(id+"F1.imprint","IMPRINT",EDGE,{"disambiguationData":[TD([[subQ4,1.0]])],"derivedFrom":subQ3}),-1.0]])]});}
            var Q13;
            {var subQ5=sQuery(id+"F1.wireOp",EDGE,"E25.4.0.0");Q13=makeQuery(id+"F1.imprint","IMPRINT",FACE,{"disambiguationData":[TD([[makeQuery(id+"F1.imprint","IMPRINT",EDGE,{"derivedFrom":subQ5}),1.0]])]});}
            var Q14;
            {var subQ5=sQuery(id+"F1.wireOp",EDGE,"E25.4.0.1");Q14=makeQuery(id+"F1.imprint","IMPRINT",FACE,{"disambiguationData":[TD([[makeQuery(id+"F1.imprint","IMPRINT",EDGE,{"derivedFrom":subQ5}),-1.0]])]});}
            var Q15;
            {var subQ0=sQuery(id+"F1.wireOp",EDGE,"E19.5.0.0");var subQ3=sQuery(id+"F1.wireOp",EDGE,"E17.bottom");var subQ4=makeQuery(id+"F1.imprint","INTERSECT",VERTEX,{"derivedFrom":[subQ3,subQ0]});Q15=makeQuery(id+"F1.imprint","IMPRINT",FACE,{"disambiguationData":[TD([[makeQuery(id+"F1.imprint","IMPRINT",EDGE,{"disambiguationData":[TD([[subQ4,1.0]])],"derivedFrom":subQ3}),-1.0]])]});}
            var Q16;
            {var subQ5=sQuery(id+"F1.wireOp",EDGE,"E25.5.0.0");Q16=makeQuery(id+"F1.imprint","IMPRINT",FACE,{"disambiguationData":[TD([[makeQuery(id+"F1.imprint","IMPRINT",EDGE,{"derivedFrom":subQ5}),1.0]])]});}
            var Q17;
            {var subQ5=sQuery(id+"F1.wireOp",EDGE,"o7LFFfXf-XPDj-YDJ7-bAYC-L3mfDlW3X8TR.bottom");Q17=makeQuery(id+"F1.imprint","IMPRINT",FACE,{"disambiguationData":[TD([[makeQuery(id+"F1.imprint","IMPRINT",EDGE,{"derivedFrom":subQ5}),1.0]])]});}
            var Q18;
            {var subQ5=sQuery(id+"F1.wireOp",EDGE,"E25.6.0.0");Q18=makeQuery(id+"F1.imprint","IMPRINT",FACE,{"disambiguationData":[TD([[makeQuery(id+"F1.imprint","IMPRINT",EDGE,{"derivedFrom":subQ5}),1.0]])]});}
            var Q19;
            Q19=makeQuery(id+"F1.imprint","IMPRINT",FACE,{"disambiguationData":[TD([[makeQuery(id+"F1.imprint","IMPRINT",EDGE,{"derivedFrom":sQuery(id+"F1.wireOp",EDGE,"E19.7.0.0")}),-1.0]])]});
            var Q20;
            {var subQ5=sQuery(id+"F1.wireOp",EDGE,"E25.6.0.1");Q20=makeQuery(id+"F1.imprint","IMPRINT",FACE,{"disambiguationData":[TD([[makeQuery(id+"F1.imprint","IMPRINT",EDGE,{"derivedFrom":subQ5}),-1.0]])]});}
            var Q21;
            {var subQ5=sQuery(id+"F1.wireOp",EDGE,"E25.5.0.1");Q21=makeQuery(id+"F1.imprint","IMPRINT",FACE,{"disambiguationData":[TD([[makeQuery(id+"F1.imprint","IMPRINT",EDGE,{"derivedFrom":subQ5}),-1.0]])]});}
            var Q22;
            {var subQ6=sQuery(id+"F1.wireOp",EDGE,"E92.top");Q22=makeQuery(id+"F1.imprint","IMPRINT",FACE,{"disambiguationData":[TD([[makeQuery(id+"F1.imprint","IMPRINT",EDGE,{"derivedFrom":subQ6}),-1.0]])]});}
            var Q23;
            {var subQ3=sQuery(id+"F1.wireOp",EDGE,"E107.bottom");Q23=makeQuery(id+"F1.imprint","IMPRINT",FACE,{"disambiguationData":[TD([[makeQuery(id+"F1.imprint","IMPRINT",EDGE,{"derivedFrom":subQ3}),-1.0]])]});}
            var Q24;
            Q24=makeQuery(id+"F1.imprint","IMPRINT",FACE,{"disambiguationData":[TD([[makeQuery(id+"F1.imprint","IMPRINT",EDGE,{"derivedFrom":sQuery(id+"F1.wireOp",EDGE,"E108.bottom")}),-1.0]])]});
            var Q25;
            {var subQ2=sQuery(id+"F1.wireOp",EDGE,"OE6oFQgg-1iZH-lJda-pF8F-zLQ9cKPHJxX8");Q25=makeQuery(id+"F1.imprint","IMPRINT",FACE,{"disambiguationData":[TD([[makeQuery(id+"F1.imprint","IMPRINT",EDGE,{"derivedFrom":subQ2}),1.0]])]});}
            var Q26;
            Q26=makeQuery(id+"F1.imprint","IMPRINT",FACE,{"disambiguationData":[TD([[makeQuery(id+"F1.imprint","IMPRINT",EDGE,{"derivedFrom":sQuery(id+"F1.wireOp",EDGE,"E109.bottom")}),1.0]])]});
            var Q27;
            {var subQ0=sQuery(id+"F1.wireOp",EDGE,"E19.6.0.0");var subQ5=sQuery(id+"F1.wireOp",EDGE,"E17.bottom");var subQ6=makeQuery(id+"F1.imprint","INTERSECT",VERTEX,{"derivedFrom":[subQ5,subQ0]});Q27=makeQuery(id+"F1.imprint","IMPRINT",FACE,{"disambiguationData":[TD([[makeQuery(id+"F1.imprint","IMPRINT",EDGE,{"disambiguationData":[TD([[subQ6,1.0]])],"derivedFrom":subQ5}),-1.0]])]});}
            var Q28;
            {var subQ3=sQuery(id+"F1.wireOp",EDGE,"E20");Q28=makeQuery(id+"F1.imprint","IMPRINT",FACE,{"disambiguationData":[TD([[makeQuery(id+"F1.imprint","IMPRINT",EDGE,{"derivedFrom":subQ3}),1.0]])]});}
            var Q29;
            {var subQ1=sQuery(id+"F1.wireOp",EDGE,"E116.left");Q29=makeQuery(id+"F1.imprint","IMPRINT",FACE,{"disambiguationData":[TD([[makeQuery(id+"F1.imprint","IMPRINT",EDGE,{"derivedFrom":subQ1}),1.0]])]});}
            var Q30;
            {var subQ5=sQuery(id+"F1.wireOp",EDGE,"E124");Q30=makeQuery(id+"F1.imprint","IMPRINT",FACE,{"disambiguationData":[TD([[makeQuery(id+"F1.imprint","IMPRINT",EDGE,{"derivedFrom":subQ5}),-1.0]])]});}
            extrude(context, id + "F4", {"entities" : qUnion([Q0, Q1, Q2, Q3, Q4, Q5, Q6, Q7, Q8, Q9, Q10, Q11, Q12, Q13, Q14, Q15, Q16, Q17, Q18, Q19, Q20, Q21, Q22, Q23, Q24, Q25, Q26, Q27, Q28, Q29, Q30]), "depth" : 18.03 * mm});
        }
        {
            var Q0;
            Q0=makeQuery(id+"F4.opExtrude","SWEPT_EDGE",EDGE,{"disambiguationData":[OSD([sQuery(id+"F1.wireOp",EDGE,"E93"),sQuery(id+"F1.wireOp",EDGE,"E120")])]});
            var Q1;
            Q1=makeQuery(id+"F4.opExtrude","SWEPT_EDGE",EDGE,{"disambiguationData":[OSD([sQuery(id+"F1.wireOp",EDGE,"E92.left"),sQuery(id+"F1.wireOp",EDGE,"E93")])]});
            var Q2;
            Q2=makeQuery(id+"F4.opExtrude","SWEPT_EDGE",EDGE,{"disambiguationData":[OSD([sQuery(id+"F1.wireOp",EDGE,"E92.right"),sQuery(id+"F1.wireOp",EDGE,"E122")])]});
            var Q3;
            Q3=makeQuery(id+"F4.opExtrude","SWEPT_EDGE",EDGE,{"disambiguationData":[OSD([sQuery(id+"F1.wireOp",EDGE,"E120"),sQuery(id+"F1.wireOp",EDGE,"E122")])]});
            fillet(context, id + "F5", {"entities" : qUnion([Q0, Q1, Q2, Q3]), "radius" : 127 * mm, "tangentPropagation" : true, "allowEdgeOverflow" : false});
        }
        {
            var Q0;
            Q0=makeQuery(id+"F4.opExtrude","SWEPT_EDGE",EDGE,{"disambiguationData":[OSD([sQuery(id+"F1.wireOp",EDGE,"E107.bottom"),sQuery(id+"F1.wireOp",EDGE,"E107.right")])]});
            fillet(context, id + "F6", {"entities" : qUnion([Q0]), "radius" : 12.7 * mm, "tangentPropagation" : true, "allowEdgeOverflow" : false});
        }
    });
